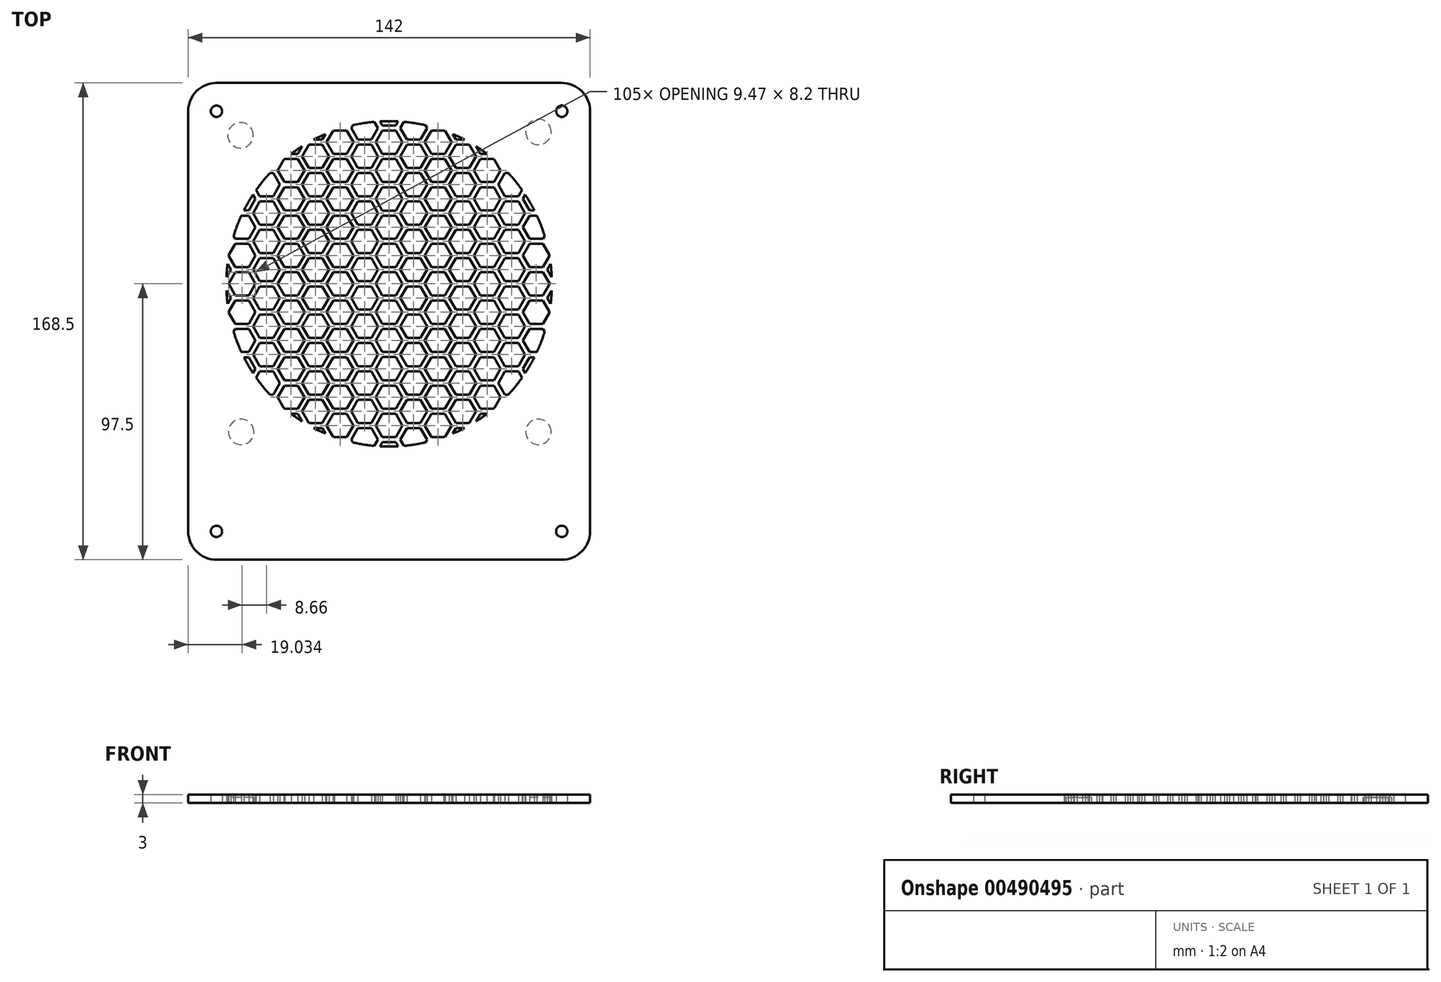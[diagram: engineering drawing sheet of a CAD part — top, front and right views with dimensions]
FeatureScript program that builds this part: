
annotation { "Feature Type Name" : "Feature", "Feature Type Description" : "" }
export const myFeature = defineFeature(function(context is Context, id is Id, definition is map)
    precondition{}
    {
        {
            var Q0;
            Q0=qCreatedBy(makeId("Top.planeOp"),FACE);
            var sketch = newSketch(context, id + "F0", { "sketchPlane" : qUnion([Q0])});
            skPoint(sketch, "E0.middle", {"position": v(0, 0) * mm});
            skLineSegment(sketch, "E1", {"start": v(-61, -92.5) * mm, "end": v(61, -92.5) * mm, "construction": true});
            skLineSegment(sketch, "E2", {"start": v(-66, 61) * mm, "end": v(-66, -87.5) * mm, "construction": true});
            skLineSegment(sketch, "E3", {"start": v(-61, 66) * mm, "end": v(61, 66) * mm, "construction": true});
            skLineSegment(sketch, "E4", {"start": v(66, 61) * mm, "end": v(66, -87.5) * mm, "construction": true});
            skArc(sketch, "E5.filletArc", {"start": v(-61, 66) * mm, "mid": v(-64.54, 64.54) * mm, "end": v(-66, 61) * mm, "construction": true});
            skArc(sketch, "E6.filletArc", {"start": v(66, 61) * mm, "mid": v(64.54, 64.54) * mm, "end": v(61, 66) * mm, "construction": true});
            skArc(sketch, "E7.converted", {"start": v(-66, -87.5) * mm, "mid": v(-64.54, -91.04) * mm, "end": v(-61, -92.5) * mm, "construction": true});
            skArc(sketch, "E8.trimOffspring", {"start": v(61, -92.5) * mm, "mid": v(64.54, -91.04) * mm, "end": v(66, -87.5) * mm, "construction": true});
            skPoint(sketch, "E9", {"position": v(-54.5, -54.5) * mm});
            skPoint(sketch, "E10", {"position": v(-54.5, 54.5) * mm});
            skPoint(sketch, "E11", {"position": v(54.5, 54.5) * mm});
            skPoint(sketch, "E12", {"position": v(54.5, -54.5) * mm});
            skLineSegment(sketch, "E13", {"start": v(-59.5, 59.5) * mm, "end": v(59.5, -59.5) * mm, "construction": true});
            skLineSegment(sketch, "E14", {"start": v(-59.5, -59.5) * mm, "end": v(59.5, 59.5) * mm, "construction": true});
            skArc(sketch, "E15", {"start": v(57.5, 0) * mm, "mid": v(57.4, 3.52) * mm, "end": v(57.07, 7.03) * mm});
            skLineSegment(sketch, "E16.0", {"start": v(3.93, 5) * mm, "end": v(6.3, 0.9) * mm});
            skLineSegment(sketch, "E16.1", {"start": v(6.3, 9.1) * mm, "end": v(11.03, 9.1) * mm});
            skLineSegment(sketch, "E16.2", {"start": v(13.4, 5) * mm, "end": v(11.03, 9.1) * mm});
            skLineSegment(sketch, "E16.3", {"start": v(3.93, 5) * mm, "end": v(6.3, 9.1) * mm});
            skLineSegment(sketch, "E16.4", {"start": v(11.03, 0.9) * mm, "end": v(13.4, 5) * mm});
            skLineSegment(sketch, "E16.5", {"start": v(6.3, 0.9) * mm, "end": v(11.03, 0.9) * mm});
            skLineSegment(sketch, "E17.1", {"start": v(14.95, 4.1) * mm, "end": v(19.69, 4.1) * mm});
            skLineSegment(sketch, "E17.2", {"start": v(22.05, 0) * mm, "end": v(19.69, 4.1) * mm});
            skLineSegment(sketch, "E17.3", {"start": v(12.59, 0) * mm, "end": v(14.95, 4.1) * mm});
            skLineSegment(sketch, "E18.0", {"start": v(21.25, 5) * mm, "end": v(23.61, 0.9) * mm});
            skLineSegment(sketch, "E18.1", {"start": v(23.61, 9.1) * mm, "end": v(28.35, 9.1) * mm});
            skLineSegment(sketch, "E18.2", {"start": v(30.72, 5) * mm, "end": v(28.35, 9.1) * mm});
            skLineSegment(sketch, "E18.3", {"start": v(21.25, 5) * mm, "end": v(23.61, 9.1) * mm});
            skLineSegment(sketch, "E18.4", {"start": v(28.35, 0.9) * mm, "end": v(30.72, 5) * mm});
            skLineSegment(sketch, "E18.5", {"start": v(23.61, 0.9) * mm, "end": v(28.35, 0.9) * mm});
            skLineSegment(sketch, "E19.1", {"start": v(32.27, 4.1) * mm, "end": v(37, 4.1) * mm});
            skLineSegment(sketch, "E19.2", {"start": v(39.38, 0) * mm, "end": v(37, 4.1) * mm});
            skLineSegment(sketch, "E19.3", {"start": v(29.9, 0) * mm, "end": v(32.27, 4.1) * mm});
            skLineSegment(sketch, "E20.0", {"start": v(38.57, 5) * mm, "end": v(40.94, 0.9) * mm});
            skLineSegment(sketch, "E20.1", {"start": v(40.94, 9.1) * mm, "end": v(45.67, 9.1) * mm});
            skLineSegment(sketch, "E20.2", {"start": v(48.04, 5) * mm, "end": v(45.67, 9.1) * mm});
            skLineSegment(sketch, "E20.3", {"start": v(38.57, 5) * mm, "end": v(40.94, 9.1) * mm});
            skLineSegment(sketch, "E20.4", {"start": v(45.67, 0.9) * mm, "end": v(48.04, 5) * mm});
            skLineSegment(sketch, "E20.5", {"start": v(40.94, 0.9) * mm, "end": v(45.67, 0.9) * mm});
            skLineSegment(sketch, "E21.1", {"start": v(49.6, 4.1) * mm, "end": v(54.33, 4.1) * mm});
            skLineSegment(sketch, "E21.2", {"start": v(56.7, 0) * mm, "end": v(54.33, 4.1) * mm});
            skLineSegment(sketch, "E21.3", {"start": v(47.23, 0) * mm, "end": v(49.6, 4.1) * mm});
            skLineSegment(sketch, "E22.0", {"start": v(55.9, 5) * mm, "end": v(57.45, 2.3) * mm});
            skLineSegment(sketch, "E22.3", {"start": v(55.9, 5) * mm, "end": v(57.07, 7.03) * mm});
            skLineSegment(sketch, "E23.1", {"start": v(0, 4.1) * mm, "end": v(2.37, 4.1) * mm});
            skLineSegment(sketch, "E23.2", {"start": v(4.73, 0) * mm, "end": v(2.37, 4.1) * mm});
            skLineSegment(sketch, "E24.1", {"start": v(0, 14.1) * mm, "end": v(2.37, 14.1) * mm});
            skLineSegment(sketch, "E24.2", {"start": v(4.73, 10) * mm, "end": v(2.37, 14.1) * mm});
            skLineSegment(sketch, "E24.4", {"start": v(2.37, 5.9) * mm, "end": v(4.73, 10) * mm});
            skLineSegment(sketch, "E24.5", {"start": v(0, 5.9) * mm, "end": v(2.37, 5.9) * mm});
            skLineSegment(sketch, "E25.0", {"start": v(3.93, 15) * mm, "end": v(6.3, 10.9) * mm});
            skLineSegment(sketch, "E25.1", {"start": v(6.3, 19.1) * mm, "end": v(11.03, 19.1) * mm});
            skLineSegment(sketch, "E25.2", {"start": v(13.4, 15) * mm, "end": v(11.03, 19.1) * mm});
            skLineSegment(sketch, "E25.3", {"start": v(3.93, 15) * mm, "end": v(6.3, 19.1) * mm});
            skLineSegment(sketch, "E25.4", {"start": v(11.03, 10.9) * mm, "end": v(13.4, 15) * mm});
            skLineSegment(sketch, "E25.5", {"start": v(6.3, 10.9) * mm, "end": v(11.03, 10.9) * mm});
            skLineSegment(sketch, "E26.0", {"start": v(12.59, 10) * mm, "end": v(14.95, 5.9) * mm});
            skLineSegment(sketch, "E26.1", {"start": v(14.95, 14.1) * mm, "end": v(19.69, 14.1) * mm});
            skLineSegment(sketch, "E26.2", {"start": v(22.05, 10) * mm, "end": v(19.69, 14.1) * mm});
            skLineSegment(sketch, "E26.3", {"start": v(12.59, 10) * mm, "end": v(14.95, 14.1) * mm});
            skLineSegment(sketch, "E26.4", {"start": v(19.69, 5.9) * mm, "end": v(22.05, 10) * mm});
            skLineSegment(sketch, "E26.5", {"start": v(14.95, 5.9) * mm, "end": v(19.69, 5.9) * mm});
            skLineSegment(sketch, "E27.0", {"start": v(21.25, 15) * mm, "end": v(23.61, 10.9) * mm});
            skLineSegment(sketch, "E27.1", {"start": v(23.61, 19.1) * mm, "end": v(28.35, 19.1) * mm});
            skLineSegment(sketch, "E27.2", {"start": v(30.72, 15) * mm, "end": v(28.35, 19.1) * mm});
            skLineSegment(sketch, "E27.3", {"start": v(21.25, 15) * mm, "end": v(23.61, 19.1) * mm});
            skLineSegment(sketch, "E27.4", {"start": v(28.35, 10.9) * mm, "end": v(30.72, 15) * mm});
            skLineSegment(sketch, "E27.5", {"start": v(23.61, 10.9) * mm, "end": v(28.35, 10.9) * mm});
            skLineSegment(sketch, "E28.0", {"start": v(29.9, 10) * mm, "end": v(32.27, 5.9) * mm});
            skLineSegment(sketch, "E28.1", {"start": v(32.27, 14.1) * mm, "end": v(37, 14.1) * mm});
            skLineSegment(sketch, "E28.2", {"start": v(39.38, 10) * mm, "end": v(37, 14.1) * mm});
            skLineSegment(sketch, "E28.3", {"start": v(29.9, 10) * mm, "end": v(32.27, 14.1) * mm});
            skLineSegment(sketch, "E28.4", {"start": v(37, 5.9) * mm, "end": v(39.38, 10) * mm});
            skLineSegment(sketch, "E28.5", {"start": v(32.27, 5.9) * mm, "end": v(37, 5.9) * mm});
            skLineSegment(sketch, "E29.0", {"start": v(38.57, 15) * mm, "end": v(40.94, 10.9) * mm});
            skLineSegment(sketch, "E29.1", {"start": v(40.94, 19.1) * mm, "end": v(45.67, 19.1) * mm});
            skLineSegment(sketch, "E29.2", {"start": v(48.04, 15) * mm, "end": v(45.67, 19.1) * mm});
            skLineSegment(sketch, "E29.3", {"start": v(38.57, 15) * mm, "end": v(40.94, 19.1) * mm});
            skLineSegment(sketch, "E29.4", {"start": v(45.67, 10.9) * mm, "end": v(48.04, 15) * mm});
            skLineSegment(sketch, "E29.5", {"start": v(40.94, 10.9) * mm, "end": v(45.67, 10.9) * mm});
            skLineSegment(sketch, "E30.0", {"start": v(47.23, 10) * mm, "end": v(49.6, 5.9) * mm});
            skLineSegment(sketch, "E30.1", {"start": v(49.6, 14.1) * mm, "end": v(54.33, 14.1) * mm});
            skLineSegment(sketch, "E30.2", {"start": v(56.59, 10.2) * mm, "end": v(54.33, 14.1) * mm});
            skLineSegment(sketch, "E30.3", {"start": v(47.23, 10) * mm, "end": v(49.6, 14.1) * mm});
            skLineSegment(sketch, "E30.4", {"start": v(54.33, 5.9) * mm, "end": v(56.64, 9.9) * mm});
            skLineSegment(sketch, "E30.5", {"start": v(49.6, 5.9) * mm, "end": v(54.33, 5.9) * mm});
            skLineSegment(sketch, "E31.1", {"start": v(0, 24.1) * mm, "end": v(2.37, 24.1) * mm});
            skLineSegment(sketch, "E31.2", {"start": v(4.73, 20) * mm, "end": v(2.37, 24.1) * mm});
            skLineSegment(sketch, "E31.4", {"start": v(2.37, 15.9) * mm, "end": v(4.73, 20) * mm});
            skLineSegment(sketch, "E31.5", {"start": v(0, 15.9) * mm, "end": v(2.37, 15.9) * mm});
            skLineSegment(sketch, "E32.0", {"start": v(3.93, 25) * mm, "end": v(6.3, 20.9) * mm});
            skLineSegment(sketch, "E32.1", {"start": v(6.3, 29.1) * mm, "end": v(11.03, 29.1) * mm});
            skLineSegment(sketch, "E32.2", {"start": v(13.4, 25) * mm, "end": v(11.03, 29.1) * mm});
            skLineSegment(sketch, "E32.3", {"start": v(3.93, 25) * mm, "end": v(6.3, 29.1) * mm});
            skLineSegment(sketch, "E32.4", {"start": v(11.03, 20.9) * mm, "end": v(13.4, 25) * mm});
            skLineSegment(sketch, "E32.5", {"start": v(6.3, 20.9) * mm, "end": v(11.03, 20.9) * mm});
            skLineSegment(sketch, "E33.0", {"start": v(12.59, 20) * mm, "end": v(14.95, 15.9) * mm});
            skLineSegment(sketch, "E33.1", {"start": v(14.95, 24.1) * mm, "end": v(19.69, 24.1) * mm});
            skLineSegment(sketch, "E33.2", {"start": v(22.05, 20) * mm, "end": v(19.69, 24.1) * mm});
            skLineSegment(sketch, "E33.3", {"start": v(12.59, 20) * mm, "end": v(14.95, 24.1) * mm});
            skLineSegment(sketch, "E33.4", {"start": v(19.69, 15.9) * mm, "end": v(22.05, 20) * mm});
            skLineSegment(sketch, "E33.5", {"start": v(14.95, 15.9) * mm, "end": v(19.69, 15.9) * mm});
            skLineSegment(sketch, "E34.0", {"start": v(21.25, 25) * mm, "end": v(23.61, 20.9) * mm});
            skLineSegment(sketch, "E34.1", {"start": v(23.61, 29.1) * mm, "end": v(28.35, 29.1) * mm});
            skLineSegment(sketch, "E34.2", {"start": v(30.72, 25) * mm, "end": v(28.35, 29.1) * mm});
            skLineSegment(sketch, "E34.3", {"start": v(21.25, 25) * mm, "end": v(23.61, 29.1) * mm});
            skLineSegment(sketch, "E34.4", {"start": v(28.35, 20.9) * mm, "end": v(30.72, 25) * mm});
            skLineSegment(sketch, "E34.5", {"start": v(23.61, 20.9) * mm, "end": v(28.35, 20.9) * mm});
            skLineSegment(sketch, "E35.0", {"start": v(29.9, 20) * mm, "end": v(32.27, 15.9) * mm});
            skLineSegment(sketch, "E35.1", {"start": v(32.27, 24.1) * mm, "end": v(37, 24.1) * mm});
            skLineSegment(sketch, "E35.2", {"start": v(39.38, 20) * mm, "end": v(37, 24.1) * mm});
            skLineSegment(sketch, "E35.3", {"start": v(29.9, 20) * mm, "end": v(32.27, 24.1) * mm});
            skLineSegment(sketch, "E35.4", {"start": v(37, 15.9) * mm, "end": v(39.38, 20) * mm});
            skLineSegment(sketch, "E35.5", {"start": v(32.27, 15.9) * mm, "end": v(37, 15.9) * mm});
            skLineSegment(sketch, "E36.0", {"start": v(38.57, 25) * mm, "end": v(40.94, 20.9) * mm});
            skLineSegment(sketch, "E36.1", {"start": v(40.94, 29.1) * mm, "end": v(45.67, 29.1) * mm});
            skLineSegment(sketch, "E36.2", {"start": v(48.04, 25) * mm, "end": v(45.67, 29.1) * mm});
            skLineSegment(sketch, "E36.3", {"start": v(38.57, 25) * mm, "end": v(40.94, 29.1) * mm});
            skLineSegment(sketch, "E36.4", {"start": v(45.67, 20.9) * mm, "end": v(48.04, 25) * mm});
            skLineSegment(sketch, "E36.5", {"start": v(40.94, 20.9) * mm, "end": v(45.67, 20.9) * mm});
            skLineSegment(sketch, "E37.0", {"start": v(47.23, 20) * mm, "end": v(49.6, 15.9) * mm});
            skLineSegment(sketch, "E37.1", {"start": v(49.6, 24.1) * mm, "end": v(52.2, 24.1) * mm});
            skLineSegment(sketch, "E37.3", {"start": v(47.23, 20) * mm, "end": v(49.6, 24.1) * mm});
            skLineSegment(sketch, "E37.4", {"start": v(54.33, 15.9) * mm, "end": v(54.94, 16.96) * mm});
            skLineSegment(sketch, "E37.5", {"start": v(49.6, 15.9) * mm, "end": v(54.33, 15.9) * mm});
            skLineSegment(sketch, "E38.1", {"start": v(0, 34.1) * mm, "end": v(2.37, 34.1) * mm});
            skLineSegment(sketch, "E38.2", {"start": v(4.73, 30) * mm, "end": v(2.37, 34.1) * mm});
            skLineSegment(sketch, "E38.4", {"start": v(2.37, 25.9) * mm, "end": v(4.73, 30) * mm});
            skLineSegment(sketch, "E38.5", {"start": v(0, 25.9) * mm, "end": v(2.37, 25.9) * mm});
            skLineSegment(sketch, "E39.0", {"start": v(3.93, 35.06) * mm, "end": v(6.3, 30.96) * mm});
            skLineSegment(sketch, "E39.1", {"start": v(6.3, 39.16) * mm, "end": v(11.03, 39.16) * mm});
            skLineSegment(sketch, "E39.2", {"start": v(13.4, 35.06) * mm, "end": v(11.03, 39.16) * mm});
            skLineSegment(sketch, "E39.3", {"start": v(3.93, 35.06) * mm, "end": v(6.3, 39.16) * mm});
            skLineSegment(sketch, "E39.4", {"start": v(11.03, 30.96) * mm, "end": v(13.4, 35.06) * mm});
            skLineSegment(sketch, "E39.5", {"start": v(6.3, 30.96) * mm, "end": v(11.03, 30.96) * mm});
            skLineSegment(sketch, "E40.0", {"start": v(12.59, 30.06) * mm, "end": v(14.95, 25.96) * mm});
            skLineSegment(sketch, "E40.1", {"start": v(14.95, 34.16) * mm, "end": v(19.69, 34.16) * mm});
            skLineSegment(sketch, "E40.2", {"start": v(22.05, 30.06) * mm, "end": v(19.69, 34.16) * mm});
            skLineSegment(sketch, "E40.3", {"start": v(12.59, 30.06) * mm, "end": v(14.95, 34.16) * mm});
            skLineSegment(sketch, "E40.4", {"start": v(19.69, 25.96) * mm, "end": v(22.05, 30.06) * mm});
            skLineSegment(sketch, "E40.5", {"start": v(14.95, 25.96) * mm, "end": v(19.69, 25.96) * mm});
            skLineSegment(sketch, "E41.0", {"start": v(21.25, 35.06) * mm, "end": v(23.61, 30.96) * mm});
            skLineSegment(sketch, "E41.1", {"start": v(23.61, 39.16) * mm, "end": v(28.35, 39.16) * mm});
            skLineSegment(sketch, "E41.2", {"start": v(30.72, 35.06) * mm, "end": v(28.35, 39.16) * mm});
            skLineSegment(sketch, "E41.3", {"start": v(21.25, 35.06) * mm, "end": v(23.61, 39.16) * mm});
            skLineSegment(sketch, "E41.4", {"start": v(28.35, 30.96) * mm, "end": v(30.72, 35.06) * mm});
            skLineSegment(sketch, "E41.5", {"start": v(23.61, 30.96) * mm, "end": v(28.35, 30.96) * mm});
            skLineSegment(sketch, "E42.0", {"start": v(29.9, 30.06) * mm, "end": v(32.27, 25.96) * mm});
            skLineSegment(sketch, "E42.1", {"start": v(32.27, 34.16) * mm, "end": v(37, 34.16) * mm});
            skLineSegment(sketch, "E42.2", {"start": v(39.38, 30.06) * mm, "end": v(37, 34.16) * mm});
            skLineSegment(sketch, "E42.3", {"start": v(29.9, 30.06) * mm, "end": v(32.27, 34.16) * mm});
            skLineSegment(sketch, "E42.4", {"start": v(37, 25.96) * mm, "end": v(39.38, 30.06) * mm});
            skLineSegment(sketch, "E42.5", {"start": v(32.27, 25.96) * mm, "end": v(37, 25.96) * mm});
            skLineSegment(sketch, "E43.0", {"start": v(38.57, 35.06) * mm, "end": v(40.94, 30.96) * mm});
            skLineSegment(sketch, "E43.1", {"start": v(40.94, 39.16) * mm, "end": v(42.1, 39.16) * mm});
            skLineSegment(sketch, "E43.3", {"start": v(38.57, 35.06) * mm, "end": v(40.94, 39.16) * mm});
            skLineSegment(sketch, "E43.4", {"start": v(45.67, 30.96) * mm, "end": v(46.96, 33.18) * mm});
            skLineSegment(sketch, "E43.5", {"start": v(40.94, 30.96) * mm, "end": v(45.67, 30.96) * mm});
            skLineSegment(sketch, "E44.0", {"start": v(47.23, 30.06) * mm, "end": v(49.6, 25.96) * mm});
            skLineSegment(sketch, "E44.3", {"start": v(47.23, 30.06) * mm, "end": v(48.08, 31.53) * mm});
            skLineSegment(sketch, "E44.5", {"start": v(49.6, 25.96) * mm, "end": v(51.3, 25.96) * mm});
            skLineSegment(sketch, "E45.1", {"start": v(0, 44.16) * mm, "end": v(2.37, 44.16) * mm});
            skLineSegment(sketch, "E45.2", {"start": v(4.73, 40.06) * mm, "end": v(2.37, 44.16) * mm});
            skLineSegment(sketch, "E45.4", {"start": v(2.37, 35.96) * mm, "end": v(4.73, 40.06) * mm});
            skLineSegment(sketch, "E45.5", {"start": v(0, 35.96) * mm, "end": v(2.37, 35.96) * mm});
            skLineSegment(sketch, "E46.0", {"start": v(3.93, 45.06) * mm, "end": v(6.3, 40.96) * mm});
            skLineSegment(sketch, "E46.1", {"start": v(6.3, 49.16) * mm, "end": v(11.03, 49.16) * mm});
            skLineSegment(sketch, "E46.2", {"start": v(13.4, 45.06) * mm, "end": v(11.03, 49.16) * mm});
            skLineSegment(sketch, "E46.3", {"start": v(3.93, 45.06) * mm, "end": v(6.3, 49.16) * mm});
            skLineSegment(sketch, "E46.4", {"start": v(11.03, 40.96) * mm, "end": v(13.4, 45.06) * mm});
            skLineSegment(sketch, "E46.5", {"start": v(6.3, 40.96) * mm, "end": v(11.03, 40.96) * mm});
            skLineSegment(sketch, "E47.0", {"start": v(12.59, 40.06) * mm, "end": v(14.95, 35.96) * mm});
            skLineSegment(sketch, "E47.1", {"start": v(14.95, 44.16) * mm, "end": v(19.69, 44.16) * mm});
            skLineSegment(sketch, "E47.2", {"start": v(22.05, 40.06) * mm, "end": v(19.69, 44.16) * mm});
            skLineSegment(sketch, "E47.3", {"start": v(12.59, 40.06) * mm, "end": v(14.95, 44.16) * mm});
            skLineSegment(sketch, "E47.4", {"start": v(19.69, 35.96) * mm, "end": v(22.05, 40.06) * mm});
            skLineSegment(sketch, "E47.5", {"start": v(14.95, 35.96) * mm, "end": v(19.69, 35.96) * mm});
            skLineSegment(sketch, "E48.0", {"start": v(21.25, 45.06) * mm, "end": v(23.61, 40.96) * mm});
            skLineSegment(sketch, "E48.1", {"start": v(23.61, 49.16) * mm, "end": v(28.35, 49.16) * mm});
            skLineSegment(sketch, "E48.2", {"start": v(30.72, 45.06) * mm, "end": v(28.35, 49.16) * mm});
            skLineSegment(sketch, "E48.3", {"start": v(21.25, 45.06) * mm, "end": v(23.61, 49.16) * mm});
            skLineSegment(sketch, "E48.4", {"start": v(28.35, 40.96) * mm, "end": v(30.72, 45.06) * mm});
            skLineSegment(sketch, "E48.5", {"start": v(23.61, 40.96) * mm, "end": v(28.35, 40.96) * mm});
            skLineSegment(sketch, "E49.0", {"start": v(29.9, 40.06) * mm, "end": v(32.27, 35.96) * mm});
            skLineSegment(sketch, "E49.1", {"start": v(32.27, 44.16) * mm, "end": v(36.83, 44.16) * mm});
            skLineSegment(sketch, "E49.2", {"start": v(39.38, 40.06) * mm, "end": v(37.18, 43.86) * mm});
            skLineSegment(sketch, "E49.3", {"start": v(29.9, 40.06) * mm, "end": v(32.27, 44.16) * mm});
            skLineSegment(sketch, "E49.4", {"start": v(37, 35.96) * mm, "end": v(39.38, 40.06) * mm});
            skLineSegment(sketch, "E49.5", {"start": v(32.27, 35.96) * mm, "end": v(37, 35.96) * mm});
            skLineSegment(sketch, "E50.1", {"start": v(0, 54.16) * mm, "end": v(2.37, 54.16) * mm});
            skLineSegment(sketch, "E50.2", {"start": v(4.73, 50.06) * mm, "end": v(2.37, 54.16) * mm});
            skLineSegment(sketch, "E50.4", {"start": v(2.37, 45.96) * mm, "end": v(4.73, 50.06) * mm});
            skLineSegment(sketch, "E50.5", {"start": v(0, 45.96) * mm, "end": v(2.37, 45.96) * mm});
            skLineSegment(sketch, "E51.0", {"start": v(3.93, 55.06) * mm, "end": v(6.3, 50.96) * mm});
            skLineSegment(sketch, "E51.2", {"start": v(13.4, 55.06) * mm, "end": v(12.82, 56.05) * mm});
            skLineSegment(sketch, "E51.3", {"start": v(3.93, 55.06) * mm, "end": v(5.2, 57.26) * mm});
            skLineSegment(sketch, "E51.4", {"start": v(11.03, 50.96) * mm, "end": v(13.4, 55.06) * mm});
            skLineSegment(sketch, "E51.5", {"start": v(6.3, 50.96) * mm, "end": v(11.03, 50.96) * mm});
            skLineSegment(sketch, "E52.0", {"start": v(12.59, 50.06) * mm, "end": v(14.95, 45.96) * mm});
            skLineSegment(sketch, "E52.1", {"start": v(14.95, 54.16) * mm, "end": v(19.32, 54.16) * mm});
            skLineSegment(sketch, "E52.2", {"start": v(22.05, 50.06) * mm, "end": v(19.79, 53.99) * mm});
            skLineSegment(sketch, "E52.3", {"start": v(12.59, 50.06) * mm, "end": v(14.95, 54.16) * mm});
            skLineSegment(sketch, "E52.4", {"start": v(19.69, 45.96) * mm, "end": v(22.05, 50.06) * mm});
            skLineSegment(sketch, "E52.5", {"start": v(14.95, 45.96) * mm, "end": v(19.69, 45.96) * mm});
            skLineSegment(sketch, "E53.0", {"start": v(22.48, 52.92) * mm, "end": v(23.61, 50.96) * mm});
            skLineSegment(sketch, "E53.5", {"start": v(23.61, 50.96) * mm, "end": v(26.64, 50.96) * mm});
            skLineSegment(sketch, "E54.0", {"start": v(30.76, 48.58) * mm, "end": v(32.27, 45.96) * mm});
            skLineSegment(sketch, "E54.5", {"start": v(32.27, 45.96) * mm, "end": v(34.56, 45.96) * mm});
            skLineSegment(sketch, "E55.MirrorCS", {"start": v(-45.67, 30.96) * mm, "end": v(-46.96, 33.18) * mm});
            skLineSegment(sketch, "E56.MirrorCS", {"start": v(-6.3, 19.1) * mm, "end": v(-11.03, 19.1) * mm});
            skLineSegment(sketch, "E57.MirrorCS", {"start": v(0, 15.9) * mm, "end": v(-2.37, 15.9) * mm});
            skLineSegment(sketch, "E58.MirrorCS", {"start": v(-28.35, 20.9) * mm, "end": v(-30.72, 25) * mm});
            skLineSegment(sketch, "E59.MirrorCS", {"start": v(-29.9, 40.06) * mm, "end": v(-32.27, 44.16) * mm});
            skLineSegment(sketch, "E60.MirrorCS", {"start": v(-14.95, 34.16) * mm, "end": v(-19.69, 34.16) * mm});
            skLineSegment(sketch, "E61.MirrorCS", {"start": v(-21.25, 15) * mm, "end": v(-23.61, 10.9) * mm});
            skLineSegment(sketch, "E62.MirrorCS", {"start": v(-40.94, 29.1) * mm, "end": v(-45.67, 29.1) * mm});
            skLineSegment(sketch, "E63.MirrorCS", {"start": v(-14.95, 5.9) * mm, "end": v(-19.69, 5.9) * mm});
            skLineSegment(sketch, "E64.MirrorCS", {"start": v(-38.57, 15) * mm, "end": v(-40.94, 19.1) * mm});
            skLineSegment(sketch, "E65.MirrorCS", {"start": v(-3.93, 45.06) * mm, "end": v(-6.3, 49.16) * mm});
            skLineSegment(sketch, "E66.MirrorCS", {"start": v(-56.59, 10.2) * mm, "end": v(-54.33, 14.1) * mm});
            skLineSegment(sketch, "E67.MirrorCS", {"start": v(-4.73, 40.06) * mm, "end": v(-2.37, 44.16) * mm});
            skLineSegment(sketch, "E68.MirrorCS", {"start": v(-11.03, 50.96) * mm, "end": v(-13.4, 55.06) * mm});
            skLineSegment(sketch, "E69.MirrorCS", {"start": v(-2.37, 45.96) * mm, "end": v(-4.73, 50.06) * mm});
            skLineSegment(sketch, "E70.MirrorCS", {"start": v(-32.27, 34.16) * mm, "end": v(-37, 34.16) * mm});
            skLineSegment(sketch, "E71.MirrorCS", {"start": v(-3.93, 35.06) * mm, "end": v(-6.3, 39.16) * mm});
            skLineSegment(sketch, "E72.MirrorCS", {"start": v(0, 35.96) * mm, "end": v(-2.37, 35.96) * mm});
            skLineSegment(sketch, "E73.MirrorCS", {"start": v(-47.23, 30.06) * mm, "end": v(-49.6, 25.96) * mm});
            skLineSegment(sketch, "E74.MirrorCS", {"start": v(-29.9, 10) * mm, "end": v(-32.27, 5.9) * mm});
            skLineSegment(sketch, "E75.MirrorCS", {"start": v(-21.25, 45.06) * mm, "end": v(-23.61, 49.16) * mm});
            skLineSegment(sketch, "E76.MirrorCS", {"start": v(-22.05, 50.06) * mm, "end": v(-19.79, 53.99) * mm});
            skLineSegment(sketch, "E77.MirrorCS", {"start": v(-37, 35.96) * mm, "end": v(-39.38, 40.06) * mm});
            skLineSegment(sketch, "E78.MirrorCS", {"start": v(-38.57, 15) * mm, "end": v(-40.94, 10.9) * mm});
            skLineSegment(sketch, "E79.MirrorCS", {"start": v(-22.05, 20) * mm, "end": v(-19.69, 24.1) * mm});
            skLineSegment(sketch, "E80.MirrorCS", {"start": v(-32.27, 5.9) * mm, "end": v(-37, 5.9) * mm});
            skLineSegment(sketch, "E81.MirrorCS", {"start": v(-39.38, 10) * mm, "end": v(-37, 14.1) * mm});
            skLineSegment(sketch, "E82.MirrorCS", {"start": v(-32.27, 45.96) * mm, "end": v(-34.56, 45.96) * mm});
            skLineSegment(sketch, "E83.MirrorCS", {"start": v(-12.59, 50.06) * mm, "end": v(-14.95, 54.16) * mm});
            skLineSegment(sketch, "E84.MirrorCS", {"start": v(-30.72, 5) * mm, "end": v(-28.35, 9.1) * mm});
            skLineSegment(sketch, "E85.MirrorCS", {"start": v(-21.25, 25) * mm, "end": v(-23.61, 20.9) * mm});
            skLineSegment(sketch, "E86.MirrorCS", {"start": v(-45.67, 20.9) * mm, "end": v(-48.04, 25) * mm});
            skLineSegment(sketch, "E87.MirrorCS", {"start": v(-40.94, 39.16) * mm, "end": v(-42.1, 39.16) * mm});
            skLineSegment(sketch, "E88.MirrorCS", {"start": v(-45.67, 10.9) * mm, "end": v(-48.04, 15) * mm});
            skLineSegment(sketch, "E89.MirrorCS", {"start": v(0, 25.9) * mm, "end": v(-2.37, 25.9) * mm});
            skLineSegment(sketch, "E90.MirrorCS", {"start": v(-22.05, 0) * mm, "end": v(-19.69, 4.1) * mm});
            skLineSegment(sketch, "E91.MirrorCS", {"start": v(-29.9, 20) * mm, "end": v(-32.27, 15.9) * mm});
            skLineSegment(sketch, "E92.MirrorCS", {"start": v(-21.25, 25) * mm, "end": v(-23.61, 29.1) * mm});
            skLineSegment(sketch, "E93.MirrorCS", {"start": v(0, 44.16) * mm, "end": v(-2.37, 44.16) * mm});
            skLineSegment(sketch, "E94.MirrorCS", {"start": v(-38.57, 35.06) * mm, "end": v(-40.94, 39.16) * mm});
            skLineSegment(sketch, "E95.MirrorCS", {"start": v(-13.4, 25) * mm, "end": v(-11.03, 29.1) * mm});
            skLineSegment(sketch, "E96.MirrorCS", {"start": v(-55.9, 5) * mm, "end": v(-57.07, 7.03) * mm});
            skLineSegment(sketch, "E97.MirrorCS", {"start": v(-47.23, 10) * mm, "end": v(-49.6, 14.1) * mm});
            skLineSegment(sketch, "E98.MirrorCS", {"start": v(-32.27, 24.1) * mm, "end": v(-37, 24.1) * mm});
            skLineSegment(sketch, "E99.MirrorCS", {"start": v(-3.93, 25) * mm, "end": v(-6.3, 20.9) * mm});
            skLineSegment(sketch, "E100.MirrorCS", {"start": v(-40.94, 0.9) * mm, "end": v(-45.67, 0.9) * mm});
            skLineSegment(sketch, "E101.MirrorCS", {"start": v(-40.94, 19.1) * mm, "end": v(-45.67, 19.1) * mm});
            skLineSegment(sketch, "E102.MirrorCS", {"start": v(-6.3, 9.1) * mm, "end": v(-11.03, 9.1) * mm});
            skLineSegment(sketch, "E103.MirrorCS", {"start": v(-49.6, 15.9) * mm, "end": v(-54.33, 15.9) * mm});
            skLineSegment(sketch, "E104.MirrorCS", {"start": v(-14.95, 25.96) * mm, "end": v(-19.69, 25.96) * mm});
            skLineSegment(sketch, "E105.MirrorCS", {"start": v(-28.35, 0.9) * mm, "end": v(-30.72, 5) * mm});
            skLineSegment(sketch, "E106.MirrorCS", {"start": v(-38.57, 25) * mm, "end": v(-40.94, 20.9) * mm});
            skLineSegment(sketch, "E107.MirrorCS", {"start": v(-19.69, 5.9) * mm, "end": v(-22.05, 10) * mm});
            skLineSegment(sketch, "E108.MirrorCS", {"start": v(0, 4.1) * mm, "end": v(-2.37, 4.1) * mm});
            skLineSegment(sketch, "E109.MirrorCS", {"start": v(-23.61, 50.96) * mm, "end": v(-26.64, 50.96) * mm});
            skLineSegment(sketch, "E110.MirrorCS", {"start": v(-48.04, 15) * mm, "end": v(-45.67, 19.1) * mm});
            skLineSegment(sketch, "E111.MirrorCS", {"start": v(-23.61, 10.9) * mm, "end": v(-28.35, 10.9) * mm});
            skLineSegment(sketch, "E112.MirrorCS", {"start": v(-3.93, 15) * mm, "end": v(-6.3, 19.1) * mm});
            skLineSegment(sketch, "E113.MirrorCS", {"start": v(-40.94, 10.9) * mm, "end": v(-45.67, 10.9) * mm});
            skLineSegment(sketch, "E114.MirrorCS", {"start": v(-47.23, 10) * mm, "end": v(-49.6, 5.9) * mm});
            skLineSegment(sketch, "E115.MirrorCS", {"start": v(-23.61, 19.1) * mm, "end": v(-28.35, 19.1) * mm});
            skLineSegment(sketch, "E116.MirrorCS", {"start": v(-54.33, 15.9) * mm, "end": v(-54.94, 16.96) * mm});
            skLineSegment(sketch, "E117.MirrorCS", {"start": v(-49.6, 24.1) * mm, "end": v(-52.2, 24.1) * mm});
            skLineSegment(sketch, "E118.MirrorCS", {"start": v(-4.73, 50.06) * mm, "end": v(-2.37, 54.16) * mm});
            skLineSegment(sketch, "E119.MirrorCS", {"start": v(-14.95, 24.1) * mm, "end": v(-19.69, 24.1) * mm});
            skLineSegment(sketch, "E120.MirrorCS", {"start": v(-11.03, 40.96) * mm, "end": v(-13.4, 45.06) * mm});
            skLineSegment(sketch, "E121.MirrorCS", {"start": v(-39.38, 40.06) * mm, "end": v(-37.18, 43.86) * mm});
            skLineSegment(sketch, "E122.MirrorCS", {"start": v(-22.05, 30.06) * mm, "end": v(-19.69, 34.16) * mm});
            skLineSegment(sketch, "E123.MirrorCS", {"start": v(-45.67, 0.9) * mm, "end": v(-48.04, 5) * mm});
            skLineSegment(sketch, "E124.MirrorCS", {"start": v(-14.95, 4.1) * mm, "end": v(-19.69, 4.1) * mm});
            skLineSegment(sketch, "E125.MirrorCS", {"start": v(-14.95, 15.9) * mm, "end": v(-19.69, 15.9) * mm});
            skLineSegment(sketch, "E126.MirrorCS", {"start": v(-30.72, 15) * mm, "end": v(-28.35, 19.1) * mm});
            skLineSegment(sketch, "E127.MirrorCS", {"start": v(-3.93, 25) * mm, "end": v(-6.3, 29.1) * mm});
            skLineSegment(sketch, "E128.MirrorCS", {"start": v(-23.61, 9.1) * mm, "end": v(-28.35, 9.1) * mm});
            skLineSegment(sketch, "E129.MirrorCS", {"start": v(-38.57, 25) * mm, "end": v(-40.94, 29.1) * mm});
            skLineSegment(sketch, "E130.MirrorCS", {"start": v(-3.93, 5) * mm, "end": v(-6.3, 0.9) * mm});
            skLineSegment(sketch, "E131.MirrorCS", {"start": v(-21.25, 5) * mm, "end": v(-23.61, 9.1) * mm});
            skLineSegment(sketch, "E132.MirrorCS", {"start": v(-23.61, 20.9) * mm, "end": v(-28.35, 20.9) * mm});
            skLineSegment(sketch, "E133.MirrorCS", {"start": v(-23.61, 30.96) * mm, "end": v(-28.35, 30.96) * mm});
            skLineSegment(sketch, "E134.MirrorCS", {"start": v(0, 45.96) * mm, "end": v(-2.37, 45.96) * mm});
            skLineSegment(sketch, "E135.MirrorCS", {"start": v(-4.73, 0) * mm, "end": v(-2.37, 4.1) * mm});
            skLineSegment(sketch, "E136.MirrorCS", {"start": v(-19.69, 25.96) * mm, "end": v(-22.05, 30.06) * mm});
            skLineSegment(sketch, "E137.MirrorCS", {"start": v(-32.27, 15.9) * mm, "end": v(-37, 15.9) * mm});
            skLineSegment(sketch, "E138.MirrorCS", {"start": v(-14.95, 35.96) * mm, "end": v(-19.69, 35.96) * mm});
            skLineSegment(sketch, "E139.MirrorCS", {"start": v(-12.59, 20) * mm, "end": v(-14.95, 15.9) * mm});
            skLineSegment(sketch, "E140.MirrorCS", {"start": v(-48.04, 5) * mm, "end": v(-45.67, 9.1) * mm});
            skLineSegment(sketch, "E141.MirrorCS", {"start": v(-47.23, 20) * mm, "end": v(-49.6, 24.1) * mm});
            skLineSegment(sketch, "E142.MirrorCS", {"start": v(-29.9, 30.06) * mm, "end": v(-32.27, 25.96) * mm});
            skLineSegment(sketch, "E143.MirrorCS", {"start": v(-3.93, 55.06) * mm, "end": v(-5.2, 57.26) * mm});
            skLineSegment(sketch, "E144.MirrorCS", {"start": v(0, 24.1) * mm, "end": v(-2.37, 24.1) * mm});
            skLineSegment(sketch, "E145.MirrorCS", {"start": v(-14.95, 14.1) * mm, "end": v(-19.69, 14.1) * mm});
            skLineSegment(sketch, "E146.MirrorCS", {"start": v(-23.61, 40.96) * mm, "end": v(-28.35, 40.96) * mm});
            skLineSegment(sketch, "E147.MirrorCS", {"start": v(-6.3, 29.1) * mm, "end": v(-11.03, 29.1) * mm});
            skLineSegment(sketch, "E148.MirrorCS", {"start": v(-49.6, 5.9) * mm, "end": v(-54.33, 5.9) * mm});
            skLineSegment(sketch, "E149.MirrorCS", {"start": v(-29.9, 30.06) * mm, "end": v(-32.27, 34.16) * mm});
            skLineSegment(sketch, "E150.MirrorCS", {"start": v(-6.3, 49.16) * mm, "end": v(-11.03, 49.16) * mm});
            skLineSegment(sketch, "E151.MirrorCS", {"start": v(-32.27, 14.1) * mm, "end": v(-37, 14.1) * mm});
            skLineSegment(sketch, "E152.MirrorCS", {"start": v(-12.59, 50.06) * mm, "end": v(-14.95, 45.96) * mm});
            skLineSegment(sketch, "E153.MirrorCS", {"start": v(-37, 5.9) * mm, "end": v(-39.38, 10) * mm});
            skLineSegment(sketch, "E154.MirrorCS", {"start": v(-28.35, 40.96) * mm, "end": v(-30.72, 45.06) * mm});
            skLineSegment(sketch, "E155.MirrorCS", {"start": v(-39.38, 30.06) * mm, "end": v(-37, 34.16) * mm});
            skLineSegment(sketch, "E156.MirrorCS", {"start": v(-21.25, 45.06) * mm, "end": v(-23.61, 40.96) * mm});
            skLineSegment(sketch, "E157.MirrorCS", {"start": v(-32.27, 35.96) * mm, "end": v(-37, 35.96) * mm});
            skLineSegment(sketch, "E158.MirrorCS", {"start": v(-40.94, 9.1) * mm, "end": v(-45.67, 9.1) * mm});
            skLineSegment(sketch, "E159.MirrorCS", {"start": v(-12.59, 40.06) * mm, "end": v(-14.95, 44.16) * mm});
            skLineSegment(sketch, "E160.MirrorCS", {"start": v(-3.93, 45.06) * mm, "end": v(-6.3, 40.96) * mm});
            skLineSegment(sketch, "E161.MirrorCS", {"start": v(-38.57, 5) * mm, "end": v(-40.94, 0.9) * mm});
            skLineSegment(sketch, "E162.MirrorCS", {"start": v(-6.3, 30.96) * mm, "end": v(-11.03, 30.96) * mm});
            skLineSegment(sketch, "E163.MirrorCS", {"start": v(-6.3, 50.96) * mm, "end": v(-11.03, 50.96) * mm});
            skLineSegment(sketch, "E164.MirrorCS", {"start": v(-47.23, 20) * mm, "end": v(-49.6, 15.9) * mm});
            skLineSegment(sketch, "E165.MirrorCS", {"start": v(-19.69, 35.96) * mm, "end": v(-22.05, 40.06) * mm});
            skLineSegment(sketch, "E166.MirrorCS", {"start": v(-54.33, 5.9) * mm, "end": v(-56.64, 9.9) * mm});
            skLineSegment(sketch, "E167.MirrorCS", {"start": v(-29.9, 0) * mm, "end": v(-32.27, 4.1) * mm});
            skLineSegment(sketch, "E168.MirrorCS", {"start": v(-23.61, 49.16) * mm, "end": v(-28.35, 49.16) * mm});
            skLineSegment(sketch, "E169.MirrorCS", {"start": v(-2.37, 25.9) * mm, "end": v(-4.73, 30) * mm});
            skLineSegment(sketch, "E170.MirrorCS", {"start": v(-12.59, 30.06) * mm, "end": v(-14.95, 34.16) * mm});
            skLineSegment(sketch, "E171.MirrorCS", {"start": v(-32.27, 4.1) * mm, "end": v(-37, 4.1) * mm});
            skLineSegment(sketch, "E172.MirrorCS", {"start": v(-38.57, 5) * mm, "end": v(-40.94, 9.1) * mm});
            skLineSegment(sketch, "E173.MirrorCS", {"start": v(-38.57, 35.06) * mm, "end": v(-40.94, 30.96) * mm});
            skLineSegment(sketch, "E174.MirrorCS", {"start": v(-13.4, 55.06) * mm, "end": v(-12.82, 56.05) * mm});
            skLineSegment(sketch, "E175.MirrorCS", {"start": v(-4.73, 10) * mm, "end": v(-2.37, 14.1) * mm});
            skLineSegment(sketch, "E176.MirrorCS", {"start": v(-49.6, 25.96) * mm, "end": v(-51.3, 25.96) * mm});
            skLineSegment(sketch, "E177.MirrorCS", {"start": v(-12.59, 0) * mm, "end": v(-14.95, 4.1) * mm});
            skLineSegment(sketch, "E178.MirrorCS", {"start": v(-12.59, 10) * mm, "end": v(-14.95, 5.9) * mm});
            skLineSegment(sketch, "E179.MirrorCS", {"start": v(-49.6, 4.1) * mm, "end": v(-54.33, 4.1) * mm});
            skLineSegment(sketch, "E180.MirrorCS", {"start": v(-40.94, 20.9) * mm, "end": v(-45.67, 20.9) * mm});
            skLineSegment(sketch, "E181.MirrorCS", {"start": v(-32.27, 44.16) * mm, "end": v(-36.83, 44.16) * mm});
            skLineSegment(sketch, "E182.MirrorCS", {"start": v(-47.23, 30.06) * mm, "end": v(-48.08, 31.53) * mm});
            skLineSegment(sketch, "E183.MirrorCS", {"start": v(0, 54.16) * mm, "end": v(-2.37, 54.16) * mm});
            skLineSegment(sketch, "E184.MirrorCS", {"start": v(-12.59, 20) * mm, "end": v(-14.95, 24.1) * mm});
            skLineSegment(sketch, "E185.MirrorCS", {"start": v(-6.3, 10.9) * mm, "end": v(-11.03, 10.9) * mm});
            skLineSegment(sketch, "E186.MirrorCS", {"start": v(-56.7, 0) * mm, "end": v(-54.33, 4.1) * mm});
            skLineSegment(sketch, "E187.MirrorCS", {"start": v(0, 14.1) * mm, "end": v(-2.37, 14.1) * mm});
            skLineSegment(sketch, "E188.MirrorCS", {"start": v(-21.25, 5) * mm, "end": v(-23.61, 0.9) * mm});
            skLineSegment(sketch, "E189.MirrorCS", {"start": v(-12.59, 10) * mm, "end": v(-14.95, 14.1) * mm});
            skLineSegment(sketch, "E190.MirrorCS", {"start": v(-19.69, 15.9) * mm, "end": v(-22.05, 20) * mm});
            skLineSegment(sketch, "E191.MirrorCS", {"start": v(-11.03, 30.96) * mm, "end": v(-13.4, 35.06) * mm});
            skLineSegment(sketch, "E192.MirrorCS", {"start": v(-3.93, 35.06) * mm, "end": v(-6.3, 30.96) * mm});
            skLineSegment(sketch, "E193.MirrorCS", {"start": v(-23.61, 29.1) * mm, "end": v(-28.35, 29.1) * mm});
            skLineSegment(sketch, "E194.MirrorCS", {"start": v(-4.73, 20) * mm, "end": v(-2.37, 24.1) * mm});
            skLineSegment(sketch, "E195.MirrorCS", {"start": v(-30.72, 45.06) * mm, "end": v(-28.35, 49.16) * mm});
            skLineSegment(sketch, "E196.MirrorCS", {"start": v(-11.03, 20.9) * mm, "end": v(-13.4, 25) * mm});
            skLineSegment(sketch, "E197.MirrorCS", {"start": v(-37, 25.96) * mm, "end": v(-39.38, 30.06) * mm});
            skLineSegment(sketch, "E198.MirrorCS", {"start": v(-21.25, 35.06) * mm, "end": v(-23.61, 39.16) * mm});
            skLineSegment(sketch, "E199.MirrorCS", {"start": v(-4.73, 30) * mm, "end": v(-2.37, 34.1) * mm});
            skLineSegment(sketch, "E200.MirrorCS", {"start": v(-37, 15.9) * mm, "end": v(-39.38, 20) * mm});
            skLineSegment(sketch, "E201.MirrorCS", {"start": v(-48.04, 25) * mm, "end": v(-45.67, 29.1) * mm});
            skLineSegment(sketch, "E202.MirrorCS", {"start": v(-2.37, 35.96) * mm, "end": v(-4.73, 40.06) * mm});
            skLineSegment(sketch, "E203.MirrorCS", {"start": v(-3.93, 55.06) * mm, "end": v(-6.3, 50.96) * mm});
            skLineSegment(sketch, "E204.MirrorCS", {"start": v(-12.59, 40.06) * mm, "end": v(-14.95, 35.96) * mm});
            skLineSegment(sketch, "E205.MirrorCS", {"start": v(-6.3, 40.96) * mm, "end": v(-11.03, 40.96) * mm});
            skLineSegment(sketch, "E206.MirrorCS", {"start": v(-6.3, 39.16) * mm, "end": v(-11.03, 39.16) * mm});
            skLineSegment(sketch, "E207.MirrorCS", {"start": v(-21.25, 15) * mm, "end": v(-23.61, 19.1) * mm});
            skLineSegment(sketch, "E208.MirrorCS", {"start": v(-14.95, 44.16) * mm, "end": v(-19.69, 44.16) * mm});
            skLineSegment(sketch, "E209.MirrorCS", {"start": v(-13.4, 15) * mm, "end": v(-11.03, 19.1) * mm});
            skLineSegment(sketch, "E210.MirrorCS", {"start": v(-2.37, 5.9) * mm, "end": v(-4.73, 10) * mm});
            skLineSegment(sketch, "E211.MirrorCS", {"start": v(-28.35, 10.9) * mm, "end": v(-30.72, 15) * mm});
            skLineSegment(sketch, "E212.MirrorCS", {"start": v(-30.72, 25) * mm, "end": v(-28.35, 29.1) * mm});
            skLineSegment(sketch, "E213.MirrorCS", {"start": v(-2.37, 15.9) * mm, "end": v(-4.73, 20) * mm});
            skLineSegment(sketch, "E214.MirrorCS", {"start": v(-6.3, 20.9) * mm, "end": v(-11.03, 20.9) * mm});
            skLineSegment(sketch, "E215.MirrorCS", {"start": v(-32.27, 25.96) * mm, "end": v(-37, 25.96) * mm});
            skLineSegment(sketch, "E216.MirrorCS", {"start": v(-6.3, 0.9) * mm, "end": v(-11.03, 0.9) * mm});
            skLineSegment(sketch, "E217.MirrorCS", {"start": v(-13.4, 5) * mm, "end": v(-11.03, 9.1) * mm});
            skLineSegment(sketch, "E218.MirrorCS", {"start": v(-30.76, 48.58) * mm, "end": v(-32.27, 45.96) * mm});
            skLineSegment(sketch, "E219.MirrorCS", {"start": v(-30.72, 35.06) * mm, "end": v(-28.35, 39.16) * mm});
            skLineSegment(sketch, "E220.MirrorCS", {"start": v(-3.93, 15) * mm, "end": v(-6.3, 10.9) * mm});
            skLineSegment(sketch, "E221.MirrorCS", {"start": v(-13.4, 35.06) * mm, "end": v(-11.03, 39.16) * mm});
            skLineSegment(sketch, "E222.MirrorCS", {"start": v(-29.9, 20) * mm, "end": v(-32.27, 24.1) * mm});
            skLineSegment(sketch, "E223.MirrorCS", {"start": v(-13.4, 45.06) * mm, "end": v(-11.03, 49.16) * mm});
            skLineSegment(sketch, "E224.MirrorCS", {"start": v(-29.9, 40.06) * mm, "end": v(-32.27, 35.96) * mm});
            skLineSegment(sketch, "E225.MirrorCS", {"start": v(-11.03, 10.9) * mm, "end": v(-13.4, 15) * mm});
            skLineSegment(sketch, "E226.MirrorCS", {"start": v(0, 34.1) * mm, "end": v(-2.37, 34.1) * mm});
            skLineSegment(sketch, "E227.MirrorCS", {"start": v(-12.59, 30.06) * mm, "end": v(-14.95, 25.96) * mm});
            skLineSegment(sketch, "E228.MirrorCS", {"start": v(-22.05, 10) * mm, "end": v(-19.69, 14.1) * mm});
            skLineSegment(sketch, "E229.MirrorCS", {"start": v(-47.23, 0) * mm, "end": v(-49.6, 4.1) * mm});
            skLineSegment(sketch, "E230.MirrorCS", {"start": v(-19.69, 45.96) * mm, "end": v(-22.05, 50.06) * mm});
            skLineSegment(sketch, "E231.MirrorCS", {"start": v(-39.38, 20) * mm, "end": v(-37, 24.1) * mm});
            skLineSegment(sketch, "E232.MirrorCS", {"start": v(-28.35, 30.96) * mm, "end": v(-30.72, 35.06) * mm});
            skLineSegment(sketch, "E233.MirrorCS", {"start": v(-23.61, 0.9) * mm, "end": v(-28.35, 0.9) * mm});
            skLineSegment(sketch, "E234.MirrorCS", {"start": v(-23.61, 39.16) * mm, "end": v(-28.35, 39.16) * mm});
            skLineSegment(sketch, "E235.MirrorCS", {"start": v(0, 5.9) * mm, "end": v(-2.37, 5.9) * mm});
            skLineSegment(sketch, "E236.MirrorCS", {"start": v(-39.38, 0) * mm, "end": v(-37, 4.1) * mm});
            skLineSegment(sketch, "E237.MirrorCS", {"start": v(-49.6, 14.1) * mm, "end": v(-54.33, 14.1) * mm});
            skLineSegment(sketch, "E238.MirrorCS", {"start": v(-22.05, 40.06) * mm, "end": v(-19.69, 44.16) * mm});
            skLineSegment(sketch, "E239.MirrorCS", {"start": v(-3.93, 5) * mm, "end": v(-6.3, 9.1) * mm});
            skLineSegment(sketch, "E240.MirrorCS", {"start": v(-29.9, 10) * mm, "end": v(-32.27, 14.1) * mm});
            skLineSegment(sketch, "E241.MirrorCS", {"start": v(-14.95, 54.16) * mm, "end": v(-19.32, 54.16) * mm});
            skLineSegment(sketch, "E242.MirrorCS", {"start": v(-11.03, 0.9) * mm, "end": v(-13.4, 5) * mm});
            skLineSegment(sketch, "E243.MirrorCS", {"start": v(-55.9, 5) * mm, "end": v(-57.45, 2.3) * mm});
            skLineSegment(sketch, "E244.MirrorCS", {"start": v(-40.94, 30.96) * mm, "end": v(-45.67, 30.96) * mm});
            skLineSegment(sketch, "E245.MirrorCS", {"start": v(-14.95, 45.96) * mm, "end": v(-19.69, 45.96) * mm});
            skLineSegment(sketch, "E246.MirrorCS", {"start": v(-21.25, 35.06) * mm, "end": v(-23.61, 30.96) * mm});
            skLineSegment(sketch, "E247.MirrorCS", {"start": v(0, -15.9) * mm, "end": v(-2.37, -15.9) * mm});
            skLineSegment(sketch, "E248.MirrorCS", {"start": v(0, -4.1) * mm, "end": v(-2.37, -4.1) * mm});
            skLineSegment(sketch, "E249.MirrorCS", {"start": v(0, -25.9) * mm, "end": v(-2.37, -25.9) * mm});
            skLineSegment(sketch, "E250.MirrorCS", {"start": v(0, -14.1) * mm, "end": v(-2.37, -14.1) * mm});
            skLineSegment(sketch, "E251.MirrorCS", {"start": v(0, -44.16) * mm, "end": v(2.37, -44.16) * mm});
            skLineSegment(sketch, "E252.MirrorCS", {"start": v(0, -35.96) * mm, "end": v(-2.37, -35.96) * mm});
            skLineSegment(sketch, "E253.MirrorCS", {"start": v(0, -34.1) * mm, "end": v(2.37, -34.1) * mm});
            skLineSegment(sketch, "E254.MirrorCS", {"start": v(0, -45.96) * mm, "end": v(2.37, -45.96) * mm});
            skLineSegment(sketch, "E255.MirrorCS", {"start": v(0, -24.1) * mm, "end": v(-2.37, -24.1) * mm});
            skLineSegment(sketch, "E256.MirrorCS", {"start": v(0, -15.9) * mm, "end": v(2.37, -15.9) * mm});
            skLineSegment(sketch, "E257.MirrorCS", {"start": v(0, -45.96) * mm, "end": v(-2.37, -45.96) * mm});
            skLineSegment(sketch, "E258.MirrorCS", {"start": v(0, -35.96) * mm, "end": v(2.37, -35.96) * mm});
            skLineSegment(sketch, "E259.MirrorCS", {"start": v(0, -5.9) * mm, "end": v(-2.37, -5.9) * mm});
            skLineSegment(sketch, "E260.MirrorCS", {"start": v(0, -25.9) * mm, "end": v(2.37, -25.9) * mm});
            skLineSegment(sketch, "E261.MirrorCS", {"start": v(0, -44.16) * mm, "end": v(-2.37, -44.16) * mm});
            skLineSegment(sketch, "E262.MirrorCS", {"start": v(0, -34.1) * mm, "end": v(-2.37, -34.1) * mm});
            skLineSegment(sketch, "E263.MirrorCS", {"start": v(0, -4.1) * mm, "end": v(2.37, -4.1) * mm});
            skLineSegment(sketch, "E264.MirrorCS", {"start": v(0, -55.96) * mm, "end": v(2.37, -55.96) * mm});
            skLineSegment(sketch, "E265.MirrorCS", {"start": v(0, -54.16) * mm, "end": v(-2.37, -54.16) * mm});
            skLineSegment(sketch, "E266.MirrorCS", {"start": v(0, -14.1) * mm, "end": v(2.37, -14.1) * mm});
            skLineSegment(sketch, "E267.MirrorCS", {"start": v(0, -24.1) * mm, "end": v(2.37, -24.1) * mm});
            skLineSegment(sketch, "E268.MirrorCS", {"start": v(0, -55.96) * mm, "end": v(-2.37, -55.96) * mm});
            skLineSegment(sketch, "E269.MirrorCS", {"start": v(0, -5.9) * mm, "end": v(2.37, -5.9) * mm});
            skLineSegment(sketch, "E270.MirrorCS", {"start": v(0, -54.16) * mm, "end": v(2.37, -54.16) * mm});
            skLineSegment(sketch, "E271.MirrorCS", {"start": v(-37, -35.96) * mm, "end": v(-39.38, -40.06) * mm});
            skLineSegment(sketch, "E272.MirrorCS", {"start": v(-14.95, -4.1) * mm, "end": v(-19.69, -4.1) * mm});
            skLineSegment(sketch, "E273.MirrorCS", {"start": v(-12.59, 0) * mm, "end": v(-14.95, -4.1) * mm});
            skLineSegment(sketch, "E274.MirrorCS", {"start": v(-14.95, -5.9) * mm, "end": v(-19.69, -5.9) * mm});
            skLineSegment(sketch, "E275.MirrorCS", {"start": v(-11.03, -0.9) * mm, "end": v(-13.4, -5) * mm});
            skLineSegment(sketch, "E276.MirrorCS", {"start": v(-39.38, -40.06) * mm, "end": v(-37.18, -43.86) * mm});
            skLineSegment(sketch, "E277.MirrorCS", {"start": v(-48.04, -15) * mm, "end": v(-45.67, -19.1) * mm});
            skLineSegment(sketch, "E278.MirrorCS", {"start": v(-28.35, -0.9) * mm, "end": v(-30.72, -5) * mm});
            skLineSegment(sketch, "E279.MirrorCS", {"start": v(47.23, -20) * mm, "end": v(49.6, -15.9) * mm});
            skLineSegment(sketch, "E280.MirrorCS", {"start": v(-11.03, -40.96) * mm, "end": v(-13.4, -45.06) * mm});
            skLineSegment(sketch, "E281.MirrorCS", {"start": v(30.72, -35.06) * mm, "end": v(28.35, -39.16) * mm});
            skLineSegment(sketch, "E282.MirrorCS", {"start": v(29.9, -40.06) * mm, "end": v(32.27, -44.16) * mm});
            skLineSegment(sketch, "E283.MirrorCS", {"start": v(49.6, -25.96) * mm, "end": v(51.3, -25.96) * mm});
            skLineSegment(sketch, "E284.MirrorCS", {"start": v(-45.67, -0.9) * mm, "end": v(-48.04, -5) * mm});
            skLineSegment(sketch, "E285.MirrorCS", {"start": v(-32.27, -44.16) * mm, "end": v(-36.83, -44.16) * mm});
            skLineSegment(sketch, "E286.MirrorCS", {"start": v(48.04, -15) * mm, "end": v(45.67, -19.1) * mm});
            skLineSegment(sketch, "E287.MirrorCS", {"start": v(40.94, -9.1) * mm, "end": v(45.67, -9.1) * mm});
            skLineSegment(sketch, "E288.MirrorCS", {"start": v(39.38, -20) * mm, "end": v(37, -24.1) * mm});
            skLineSegment(sketch, "E289.MirrorCS", {"start": v(-19.69, -25.96) * mm, "end": v(-22.05, -30.06) * mm});
            skLineSegment(sketch, "E290.MirrorCS", {"start": v(21.25, -15) * mm, "end": v(23.61, -10.9) * mm});
            skLineSegment(sketch, "E291.MirrorCS", {"start": v(-12.59, -50.06) * mm, "end": v(-14.95, -45.96) * mm});
            skLineSegment(sketch, "E292.MirrorCS", {"start": v(-6.3, -9.1) * mm, "end": v(-11.03, -9.1) * mm});
            skLineSegment(sketch, "E293.MirrorCS", {"start": v(32.27, -4.1) * mm, "end": v(37, -4.1) * mm});
            skLineSegment(sketch, "E294.MirrorCS", {"start": v(14.95, -54.16) * mm, "end": v(19.32, -54.16) * mm});
            skLineSegment(sketch, "E295.MirrorCS", {"start": v(-21.25, -45.06) * mm, "end": v(-23.61, -49.16) * mm});
            skLineSegment(sketch, "E296.MirrorCS", {"start": v(-29.9, -40.06) * mm, "end": v(-32.27, -44.16) * mm});
            skLineSegment(sketch, "E297.MirrorCS", {"start": v(-12.59, -20) * mm, "end": v(-14.95, -24.1) * mm});
            skLineSegment(sketch, "E298.MirrorCS", {"start": v(-6.3, -0.9) * mm, "end": v(-11.03, -0.9) * mm});
            skLineSegment(sketch, "E299.MirrorCS", {"start": v(12.59, -30.06) * mm, "end": v(14.95, -25.96) * mm});
            skLineSegment(sketch, "E300.MirrorCS", {"start": v(-23.61, -49.16) * mm, "end": v(-28.35, -49.16) * mm});
            skLineSegment(sketch, "E301.MirrorCS", {"start": v(-37, -15.9) * mm, "end": v(-39.38, -20) * mm});
            skLineSegment(sketch, "E302.MirrorCS", {"start": v(30.76, -48.58) * mm, "end": v(32.27, -45.96) * mm});
            skLineSegment(sketch, "E303.MirrorCS", {"start": v(-49.6, -5.9) * mm, "end": v(-54.33, -5.9) * mm});
            skLineSegment(sketch, "E304.MirrorCS", {"start": v(3.93, -55.06) * mm, "end": v(6.3, -50.96) * mm});
            skLineSegment(sketch, "E305.MirrorCS", {"start": v(-13.4, -5) * mm, "end": v(-11.03, -9.1) * mm});
            skLineSegment(sketch, "E306.MirrorCS", {"start": v(-6.3, -19.1) * mm, "end": v(-11.03, -19.1) * mm});
            skLineSegment(sketch, "E307.MirrorCS", {"start": v(30.72, -15) * mm, "end": v(28.35, -19.1) * mm});
            skLineSegment(sketch, "E308.MirrorCS", {"start": v(-6.3, -29.1) * mm, "end": v(-11.03, -29.1) * mm});
            skLineSegment(sketch, "E309.MirrorCS", {"start": v(-23.61, -29.1) * mm, "end": v(-28.35, -29.1) * mm});
            skLineSegment(sketch, "E310.MirrorCS", {"start": v(32.27, -34.16) * mm, "end": v(37, -34.16) * mm});
            skLineSegment(sketch, "E311.MirrorCS", {"start": v(40.94, -30.96) * mm, "end": v(45.67, -30.96) * mm});
            skLineSegment(sketch, "E312.MirrorCS", {"start": v(-47.23, -10) * mm, "end": v(-49.6, -14.1) * mm});
            skLineSegment(sketch, "E313.MirrorCS", {"start": v(-49.6, -4.1) * mm, "end": v(-54.33, -4.1) * mm});
            skLineSegment(sketch, "E314.MirrorCS", {"start": v(3.93, -5) * mm, "end": v(6.3, -9.1) * mm});
            skLineSegment(sketch, "E315.MirrorCS", {"start": v(-12.59, -10) * mm, "end": v(-14.95, -5.9) * mm});
            skLineSegment(sketch, "E316.MirrorCS", {"start": v(11.03, -10.9) * mm, "end": v(13.4, -15) * mm});
            skLineSegment(sketch, "E317.MirrorCS", {"start": v(-23.61, -40.96) * mm, "end": v(-28.35, -40.96) * mm});
            skLineSegment(sketch, "E318.MirrorCS", {"start": v(-28.35, -30.96) * mm, "end": v(-30.72, -35.06) * mm});
            skLineSegment(sketch, "E319.MirrorCS", {"start": v(37, -25.96) * mm, "end": v(39.38, -30.06) * mm});
            skLineSegment(sketch, "E320.MirrorCS", {"start": v(13.4, -45.06) * mm, "end": v(11.03, -49.16) * mm});
            skLineSegment(sketch, "E321.MirrorCS", {"start": v(29.9, -40.06) * mm, "end": v(32.27, -35.96) * mm});
            skLineSegment(sketch, "E322.MirrorCS", {"start": v(29.9, -10) * mm, "end": v(32.27, -14.1) * mm});
            skLineSegment(sketch, "E323.MirrorCS", {"start": v(4.73, -20) * mm, "end": v(2.37, -24.1) * mm});
            skLineSegment(sketch, "E324.MirrorCS", {"start": v(14.95, -4.1) * mm, "end": v(19.69, -4.1) * mm});
            skLineSegment(sketch, "E325.MirrorCS", {"start": v(40.94, -20.9) * mm, "end": v(45.67, -20.9) * mm});
            skLineSegment(sketch, "E326.MirrorCS", {"start": v(23.61, -29.1) * mm, "end": v(28.35, -29.1) * mm});
            skLineSegment(sketch, "E327.MirrorCS", {"start": v(12.59, 0) * mm, "end": v(14.95, -4.1) * mm});
            skLineSegment(sketch, "E328.MirrorCS", {"start": v(13.4, -35.06) * mm, "end": v(11.03, -39.16) * mm});
            skLineSegment(sketch, "E329.MirrorCS", {"start": v(-29.9, -30.06) * mm, "end": v(-32.27, -25.96) * mm});
            skLineSegment(sketch, "E330.MirrorCS", {"start": v(6.3, -10.9) * mm, "end": v(11.03, -10.9) * mm});
            skLineSegment(sketch, "E331.MirrorCS", {"start": v(49.6, -4.1) * mm, "end": v(54.33, -4.1) * mm});
            skLineSegment(sketch, "E332.MirrorCS", {"start": v(56.7, 0) * mm, "end": v(54.33, -4.1) * mm});
            skLineSegment(sketch, "E333.MirrorCS", {"start": v(-21.25, -35.06) * mm, "end": v(-23.61, -30.96) * mm});
            skLineSegment(sketch, "E334.MirrorCS", {"start": v(-39.38, -20) * mm, "end": v(-37, -24.1) * mm});
            skLineSegment(sketch, "E335.MirrorCS", {"start": v(4.73, -40.06) * mm, "end": v(2.37, -44.16) * mm});
            skLineSegment(sketch, "E336.MirrorCS", {"start": v(-48.04, -5) * mm, "end": v(-45.67, -9.1) * mm});
            skLineSegment(sketch, "E337.MirrorCS", {"start": v(38.57, -15) * mm, "end": v(40.94, -10.9) * mm});
            skLineSegment(sketch, "E338.MirrorCS", {"start": v(22.05, -10) * mm, "end": v(19.69, -14.1) * mm});
            skLineSegment(sketch, "E339.MirrorCS", {"start": v(-47.23, -30.06) * mm, "end": v(-48.08, -31.53) * mm});
            skLineSegment(sketch, "E340.MirrorCS", {"start": v(28.35, -0.9) * mm, "end": v(30.72, -5) * mm});
            skLineSegment(sketch, "E341.MirrorCS", {"start": v(-12.59, -50.06) * mm, "end": v(-14.95, -54.16) * mm});
            skLineSegment(sketch, "E342.MirrorCS", {"start": v(56.59, -10.2) * mm, "end": v(54.33, -14.1) * mm});
            skLineSegment(sketch, "E343.MirrorCS", {"start": v(32.27, -14.1) * mm, "end": v(37, -14.1) * mm});
            skLineSegment(sketch, "E344.MirrorCS", {"start": v(13.4, -5) * mm, "end": v(11.03, -9.1) * mm});
            skLineSegment(sketch, "E345.MirrorCS", {"start": v(55.9, -5) * mm, "end": v(57.45, -2.3) * mm});
            skLineSegment(sketch, "E346.MirrorCS", {"start": v(-13.4, -25) * mm, "end": v(-11.03, -29.1) * mm});
            skLineSegment(sketch, "E347.MirrorCS", {"start": v(-22.05, -40.06) * mm, "end": v(-19.69, -44.16) * mm});
            skLineSegment(sketch, "E348.MirrorCS", {"start": v(-38.57, -25) * mm, "end": v(-40.94, -20.9) * mm});
            skLineSegment(sketch, "E349.MirrorCS", {"start": v(30.72, -5) * mm, "end": v(28.35, -9.1) * mm});
            skLineSegment(sketch, "E350.MirrorCS", {"start": v(6.3, -9.1) * mm, "end": v(11.03, -9.1) * mm});
            skLineSegment(sketch, "E351.MirrorCS", {"start": v(4.73, -10) * mm, "end": v(2.37, -14.1) * mm});
            skLineSegment(sketch, "E352.MirrorCS", {"start": v(22.05, -30.06) * mm, "end": v(19.69, -34.16) * mm});
            skLineSegment(sketch, "E353.MirrorCS", {"start": v(-14.95, -54.16) * mm, "end": v(-19.32, -54.16) * mm});
            skLineSegment(sketch, "E354.MirrorCS", {"start": v(-32.27, -35.96) * mm, "end": v(-37, -35.96) * mm});
            skLineSegment(sketch, "E355.MirrorCS", {"start": v(-21.25, -15) * mm, "end": v(-23.61, -10.9) * mm});
            skLineSegment(sketch, "E356.MirrorCS", {"start": v(-38.57, -15) * mm, "end": v(-40.94, -19.1) * mm});
            skLineSegment(sketch, "E357.MirrorCS", {"start": v(-3.93, -45.06) * mm, "end": v(-6.3, -40.96) * mm});
            skLineSegment(sketch, "E358.MirrorCS", {"start": v(-4.73, -10) * mm, "end": v(-2.37, -14.1) * mm});
            skLineSegment(sketch, "E359.MirrorCS", {"start": v(40.94, -10.9) * mm, "end": v(45.67, -10.9) * mm});
            skLineSegment(sketch, "E360.MirrorCS", {"start": v(49.6, -24.1) * mm, "end": v(52.2, -24.1) * mm});
            skLineSegment(sketch, "E361.MirrorCS", {"start": v(23.61, -39.16) * mm, "end": v(28.35, -39.16) * mm});
            skLineSegment(sketch, "E362.MirrorCS", {"start": v(12.59, -20) * mm, "end": v(14.95, -24.1) * mm});
            skLineSegment(sketch, "E363.MirrorCS", {"start": v(-12.59, -40.06) * mm, "end": v(-14.95, -44.16) * mm});
            skLineSegment(sketch, "E364.MirrorCS", {"start": v(-6.3, -20.9) * mm, "end": v(-11.03, -20.9) * mm});
            skLineSegment(sketch, "E365.MirrorCS", {"start": v(39.38, -40.06) * mm, "end": v(37.18, -43.86) * mm});
            skLineSegment(sketch, "E366.MirrorCS", {"start": v(-3.93, -55.06) * mm, "end": v(-5.2, -57.26) * mm});
            skLineSegment(sketch, "E367.MirrorCS", {"start": v(-14.95, -15.9) * mm, "end": v(-19.69, -15.9) * mm});
            skLineSegment(sketch, "E368.MirrorCS", {"start": v(-40.94, -0.9) * mm, "end": v(-45.67, -0.9) * mm});
            skLineSegment(sketch, "E369.MirrorCS", {"start": v(21.25, -25) * mm, "end": v(23.61, -29.1) * mm});
            skLineSegment(sketch, "E370.MirrorCS", {"start": v(45.67, -0.9) * mm, "end": v(48.04, -5) * mm});
            skLineSegment(sketch, "E371.MirrorCS", {"start": v(-3.93, -25) * mm, "end": v(-6.3, -29.1) * mm});
            skLineSegment(sketch, "E372.MirrorCS", {"start": v(-3.93, -5) * mm, "end": v(-6.3, -9.1) * mm});
            skLineSegment(sketch, "E373.MirrorCS", {"start": v(-13.4, -45.06) * mm, "end": v(-11.03, -49.16) * mm});
            skLineSegment(sketch, "E374.MirrorCS", {"start": v(6.3, -20.9) * mm, "end": v(11.03, -20.9) * mm});
            skLineSegment(sketch, "E375.MirrorCS", {"start": v(-14.95, -14.1) * mm, "end": v(-19.69, -14.1) * mm});
            skLineSegment(sketch, "E376.MirrorCS", {"start": v(38.57, -5) * mm, "end": v(40.94, -0.9) * mm});
            skLineSegment(sketch, "E377.MirrorCS", {"start": v(-14.95, -44.16) * mm, "end": v(-19.69, -44.16) * mm});
            skLineSegment(sketch, "E378.MirrorCS", {"start": v(37, -35.96) * mm, "end": v(39.38, -40.06) * mm});
            skLineSegment(sketch, "E379.MirrorCS", {"start": v(40.94, -39.16) * mm, "end": v(42.1, -39.16) * mm});
            skLineSegment(sketch, "E380.MirrorCS", {"start": v(6.3, -50.96) * mm, "end": v(11.03, -50.96) * mm});
            skLineSegment(sketch, "E381.MirrorCS", {"start": v(-21.25, -15) * mm, "end": v(-23.61, -19.1) * mm});
            skLineSegment(sketch, "E382.MirrorCS", {"start": v(6.3, -19.1) * mm, "end": v(11.03, -19.1) * mm});
            skLineSegment(sketch, "E383.MirrorCS", {"start": v(37, -5.9) * mm, "end": v(39.38, -10) * mm});
            skLineSegment(sketch, "E384.MirrorCS", {"start": v(-55.9, -5) * mm, "end": v(-57.07, -7.03) * mm});
            skLineSegment(sketch, "E385.MirrorCS", {"start": v(11.03, -50.96) * mm, "end": v(13.4, -55.06) * mm});
            skLineSegment(sketch, "E386.MirrorCS", {"start": v(-30.72, -25) * mm, "end": v(-28.35, -29.1) * mm});
            skLineSegment(sketch, "E387.MirrorCS", {"start": v(-3.93, -55.06) * mm, "end": v(-6.3, -50.96) * mm});
            skLineSegment(sketch, "E388.MirrorCS", {"start": v(22.05, -20) * mm, "end": v(19.69, -24.1) * mm});
            skLineSegment(sketch, "E389.MirrorCS", {"start": v(2.37, -35.96) * mm, "end": v(4.73, -40.06) * mm});
            skLineSegment(sketch, "E390.MirrorCS", {"start": v(-32.27, -45.96) * mm, "end": v(-34.56, -45.96) * mm});
            skLineSegment(sketch, "E391.MirrorCS", {"start": v(-21.25, -5) * mm, "end": v(-23.61, -0.9) * mm});
            skLineSegment(sketch, "E392.MirrorCS", {"start": v(39.38, -30.06) * mm, "end": v(37, -34.16) * mm});
            skLineSegment(sketch, "E393.MirrorCS", {"start": v(3.93, -45.06) * mm, "end": v(6.3, -40.96) * mm});
            skLineSegment(sketch, "E394.MirrorCS", {"start": v(-21.25, -5) * mm, "end": v(-23.61, -9.1) * mm});
            skLineSegment(sketch, "E395.MirrorCS", {"start": v(14.95, -34.16) * mm, "end": v(19.69, -34.16) * mm});
            skLineSegment(sketch, "E396.MirrorCS", {"start": v(-39.38, -10) * mm, "end": v(-37, -14.1) * mm});
            skLineSegment(sketch, "E397.MirrorCS", {"start": v(-23.61, -20.9) * mm, "end": v(-28.35, -20.9) * mm});
            skLineSegment(sketch, "E398.MirrorCS", {"start": v(-12.59, -30.06) * mm, "end": v(-14.95, -34.16) * mm});
            skLineSegment(sketch, "E399.MirrorCS", {"start": v(38.57, -5) * mm, "end": v(40.94, -9.1) * mm});
            skLineSegment(sketch, "E400.MirrorCS", {"start": v(-6.3, -40.96) * mm, "end": v(-11.03, -40.96) * mm});
            skLineSegment(sketch, "E401.MirrorCS", {"start": v(-40.94, -29.1) * mm, "end": v(-45.67, -29.1) * mm});
            skLineSegment(sketch, "E402.MirrorCS", {"start": v(-11.03, -30.96) * mm, "end": v(-13.4, -35.06) * mm});
            skLineSegment(sketch, "E403.MirrorCS", {"start": v(-3.93, -45.06) * mm, "end": v(-6.3, -49.16) * mm});
            skLineSegment(sketch, "E404.MirrorCS", {"start": v(30.72, -45.06) * mm, "end": v(28.35, -49.16) * mm});
            skLineSegment(sketch, "E405.MirrorCS", {"start": v(2.37, -45.96) * mm, "end": v(4.73, -50.06) * mm});
            skLineSegment(sketch, "E406.MirrorCS", {"start": v(-32.27, -5.9) * mm, "end": v(-37, -5.9) * mm});
            skLineSegment(sketch, "E407.MirrorCS", {"start": v(12.59, -10) * mm, "end": v(14.95, -5.9) * mm});
            skLineSegment(sketch, "E408.MirrorCS", {"start": v(-40.94, -30.96) * mm, "end": v(-45.67, -30.96) * mm});
            skLineSegment(sketch, "E409.MirrorCS", {"start": v(2.37, -55.96) * mm, "end": v(3.2, -57.41) * mm});
            skLineSegment(sketch, "E410.MirrorCS", {"start": v(3.93, -15) * mm, "end": v(6.3, -10.9) * mm});
            skLineSegment(sketch, "E411.MirrorCS", {"start": v(40.94, -29.1) * mm, "end": v(45.67, -29.1) * mm});
            skLineSegment(sketch, "E412.MirrorCS", {"start": v(-6.3, -39.16) * mm, "end": v(-11.03, -39.16) * mm});
            skLineSegment(sketch, "E413.MirrorCS", {"start": v(19.69, -25.96) * mm, "end": v(22.05, -30.06) * mm});
            skLineSegment(sketch, "E414.MirrorCS", {"start": v(38.57, -35.06) * mm, "end": v(40.94, -39.16) * mm});
            skLineSegment(sketch, "E415.MirrorCS", {"start": v(-22.05, 0) * mm, "end": v(-19.69, -4.1) * mm});
            skLineSegment(sketch, "E416.MirrorCS", {"start": v(-6.3, -49.16) * mm, "end": v(-11.03, -49.16) * mm});
            skLineSegment(sketch, "E417.MirrorCS", {"start": v(-47.23, -10) * mm, "end": v(-49.6, -5.9) * mm});
            skLineSegment(sketch, "E418.MirrorCS", {"start": v(-13.4, -35.06) * mm, "end": v(-11.03, -39.16) * mm});
            skLineSegment(sketch, "E419.MirrorCS", {"start": v(22.05, -50.06) * mm, "end": v(19.79, -53.99) * mm});
            skLineSegment(sketch, "E420.MirrorCS", {"start": v(2.37, -25.9) * mm, "end": v(4.73, -30) * mm});
            skLineSegment(sketch, "E421.MirrorCS", {"start": v(28.35, -40.96) * mm, "end": v(30.72, -45.06) * mm});
            skLineSegment(sketch, "E422.MirrorCS", {"start": v(-23.61, -0.9) * mm, "end": v(-28.35, -0.9) * mm});
            skLineSegment(sketch, "E423.MirrorCS", {"start": v(32.27, -5.9) * mm, "end": v(37, -5.9) * mm});
            skLineSegment(sketch, "E424.MirrorCS", {"start": v(-29.9, -40.06) * mm, "end": v(-32.27, -35.96) * mm});
            skLineSegment(sketch, "E425.MirrorCS", {"start": v(-23.61, -30.96) * mm, "end": v(-28.35, -30.96) * mm});
            skLineSegment(sketch, "E426.MirrorCS", {"start": v(54.33, -15.9) * mm, "end": v(54.94, -16.96) * mm});
            skLineSegment(sketch, "E427.MirrorCS", {"start": v(-21.25, -25) * mm, "end": v(-23.61, -20.9) * mm});
            skLineSegment(sketch, "E428.MirrorCS", {"start": v(-38.57, -5) * mm, "end": v(-40.94, -0.9) * mm});
            skLineSegment(sketch, "E429.MirrorCS", {"start": v(22.05, 0) * mm, "end": v(19.69, -4.1) * mm});
            skLineSegment(sketch, "E430.MirrorCS", {"start": v(-30.72, -15) * mm, "end": v(-28.35, -19.1) * mm});
            skLineSegment(sketch, "E431.MirrorCS", {"start": v(-29.9, -20) * mm, "end": v(-32.27, -24.1) * mm});
            skLineSegment(sketch, "E432.MirrorCS", {"start": v(-32.27, -4.1) * mm, "end": v(-37, -4.1) * mm});
            skLineSegment(sketch, "E433.MirrorCS", {"start": v(-4.73, -20) * mm, "end": v(-2.37, -24.1) * mm});
            skLineSegment(sketch, "E434.MirrorCS", {"start": v(-14.95, -45.96) * mm, "end": v(-19.69, -45.96) * mm});
            skLineSegment(sketch, "E435.MirrorCS", {"start": v(12.59, -20) * mm, "end": v(14.95, -15.9) * mm});
            skLineSegment(sketch, "E436.MirrorCS", {"start": v(-49.6, -25.96) * mm, "end": v(-51.3, -25.96) * mm});
            skLineSegment(sketch, "E437.MirrorCS", {"start": v(29.9, -20) * mm, "end": v(32.27, -24.1) * mm});
            skLineSegment(sketch, "E438.MirrorCS", {"start": v(-28.35, -40.96) * mm, "end": v(-30.72, -45.06) * mm});
            skLineSegment(sketch, "E439.MirrorCS", {"start": v(-11.03, -10.9) * mm, "end": v(-13.4, -15) * mm});
            skLineSegment(sketch, "E440.MirrorCS", {"start": v(-6.3, -50.96) * mm, "end": v(-11.03, -50.96) * mm});
            skLineSegment(sketch, "E441.MirrorCS", {"start": v(21.25, -35.06) * mm, "end": v(23.61, -39.16) * mm});
            skLineSegment(sketch, "E442.MirrorCS", {"start": v(29.9, -10) * mm, "end": v(32.27, -5.9) * mm});
            skLineSegment(sketch, "E443.MirrorCS", {"start": v(-30.72, -45.06) * mm, "end": v(-28.35, -49.16) * mm});
            skLineSegment(sketch, "E444.MirrorCS", {"start": v(-56.7, 0) * mm, "end": v(-54.33, -4.1) * mm});
            skLineSegment(sketch, "E445.MirrorCS", {"start": v(14.95, -44.16) * mm, "end": v(19.69, -44.16) * mm});
            skLineSegment(sketch, "E446.MirrorCS", {"start": v(32.27, -15.9) * mm, "end": v(37, -15.9) * mm});
            skLineSegment(sketch, "E447.MirrorCS", {"start": v(-47.23, -20) * mm, "end": v(-49.6, -15.9) * mm});
            skLineSegment(sketch, "E448.MirrorCS", {"start": v(45.67, -20.9) * mm, "end": v(48.04, -25) * mm});
            skLineSegment(sketch, "E449.MirrorCS", {"start": v(-12.59, -10) * mm, "end": v(-14.95, -14.1) * mm});
            skLineSegment(sketch, "E450.MirrorCS", {"start": v(47.23, -30.06) * mm, "end": v(48.08, -31.53) * mm});
            skLineSegment(sketch, "E451.MirrorCS", {"start": v(-23.61, -9.1) * mm, "end": v(-28.35, -9.1) * mm});
            skLineSegment(sketch, "E452.MirrorCS", {"start": v(32.27, -25.96) * mm, "end": v(37, -25.96) * mm});
            skLineSegment(sketch, "E453.MirrorCS", {"start": v(6.3, -29.1) * mm, "end": v(11.03, -29.1) * mm});
            skLineSegment(sketch, "E454.MirrorCS", {"start": v(32.27, -44.16) * mm, "end": v(36.83, -44.16) * mm});
            skLineSegment(sketch, "E455.MirrorCS", {"start": v(30.72, -25) * mm, "end": v(28.35, -29.1) * mm});
            skLineSegment(sketch, "E456.MirrorCS", {"start": v(32.27, -35.96) * mm, "end": v(37, -35.96) * mm});
            skLineSegment(sketch, "E457.MirrorCS", {"start": v(12.59, -40.06) * mm, "end": v(14.95, -44.16) * mm});
            skLineSegment(sketch, "E458.MirrorCS", {"start": v(14.95, -35.96) * mm, "end": v(19.69, -35.96) * mm});
            skLineSegment(sketch, "E459.MirrorCS", {"start": v(3.93, -55.06) * mm, "end": v(5.2, -57.26) * mm});
            skLineSegment(sketch, "E460.MirrorCS", {"start": v(-32.27, -34.16) * mm, "end": v(-37, -34.16) * mm});
            skLineSegment(sketch, "E461.MirrorCS", {"start": v(-2.37, -15.9) * mm, "end": v(-4.73, -20) * mm});
            skLineSegment(sketch, "E462.MirrorCS", {"start": v(-23.61, -50.96) * mm, "end": v(-26.64, -50.96) * mm});
            skLineSegment(sketch, "E463.MirrorCS", {"start": v(37, -15.9) * mm, "end": v(39.38, -20) * mm});
            skLineSegment(sketch, "E464.MirrorCS", {"start": v(-38.57, -35.06) * mm, "end": v(-40.94, -30.96) * mm});
            skLineSegment(sketch, "E465.MirrorCS", {"start": v(-40.94, -10.9) * mm, "end": v(-45.67, -10.9) * mm});
            skLineSegment(sketch, "E466.MirrorCS", {"start": v(-55.9, -5) * mm, "end": v(-57.45, -2.3) * mm});
            skLineSegment(sketch, "E467.MirrorCS", {"start": v(49.6, -5.9) * mm, "end": v(54.33, -5.9) * mm});
            skLineSegment(sketch, "E468.MirrorCS", {"start": v(3.93, -5) * mm, "end": v(6.3, -0.9) * mm});
            skLineSegment(sketch, "E469.MirrorCS", {"start": v(-12.59, -20) * mm, "end": v(-14.95, -15.9) * mm});
            skLineSegment(sketch, "E470.MirrorCS", {"start": v(-21.25, -45.06) * mm, "end": v(-23.61, -40.96) * mm});
            skLineSegment(sketch, "E471.MirrorCS", {"start": v(-21.25, -25) * mm, "end": v(-23.61, -29.1) * mm});
            skLineSegment(sketch, "E472.MirrorCS", {"start": v(3.93, -35.06) * mm, "end": v(6.3, -39.16) * mm});
            skLineSegment(sketch, "E473.MirrorCS", {"start": v(-2.37, -5.9) * mm, "end": v(-4.73, -10) * mm});
            skLineSegment(sketch, "E474.MirrorCS", {"start": v(-29.9, -10) * mm, "end": v(-32.27, -14.1) * mm});
            skLineSegment(sketch, "E475.MirrorCS", {"start": v(23.61, -9.1) * mm, "end": v(28.35, -9.1) * mm});
            skLineSegment(sketch, "E476.MirrorCS", {"start": v(-2.37, -35.96) * mm, "end": v(-4.73, -40.06) * mm});
            skLineSegment(sketch, "E477.MirrorCS", {"start": v(45.67, -10.9) * mm, "end": v(48.04, -15) * mm});
            skLineSegment(sketch, "E478.MirrorCS", {"start": v(-19.69, -5.9) * mm, "end": v(-22.05, -10) * mm});
            skLineSegment(sketch, "E479.MirrorCS", {"start": v(-39.38, 0) * mm, "end": v(-37, -4.1) * mm});
            skLineSegment(sketch, "E480.MirrorCS", {"start": v(-30.76, -48.58) * mm, "end": v(-32.27, -45.96) * mm});
            skLineSegment(sketch, "E481.MirrorCS", {"start": v(-37, -25.96) * mm, "end": v(-39.38, -30.06) * mm});
            skLineSegment(sketch, "E482.MirrorCS", {"start": v(-3.93, -25) * mm, "end": v(-6.3, -20.9) * mm});
            skLineSegment(sketch, "E483.MirrorCS", {"start": v(11.03, -20.9) * mm, "end": v(13.4, -25) * mm});
            skLineSegment(sketch, "E484.MirrorCS", {"start": v(21.25, -35.06) * mm, "end": v(23.61, -30.96) * mm});
            skLineSegment(sketch, "E485.MirrorCS", {"start": v(40.94, -19.1) * mm, "end": v(45.67, -19.1) * mm});
            skLineSegment(sketch, "E486.MirrorCS", {"start": v(-22.05, -30.06) * mm, "end": v(-19.69, -34.16) * mm});
            skLineSegment(sketch, "E487.MirrorCS", {"start": v(47.23, 0) * mm, "end": v(49.6, -4.1) * mm});
            skLineSegment(sketch, "E488.MirrorCS", {"start": v(2.37, -15.9) * mm, "end": v(4.73, -20) * mm});
            skLineSegment(sketch, "E489.MirrorCS", {"start": v(23.61, -0.9) * mm, "end": v(28.35, -0.9) * mm});
            skLineSegment(sketch, "E490.MirrorCS", {"start": v(14.95, -45.96) * mm, "end": v(19.69, -45.96) * mm});
            skLineSegment(sketch, "E491.MirrorCS", {"start": v(12.59, -30.06) * mm, "end": v(14.95, -34.16) * mm});
            skLineSegment(sketch, "E492.MirrorCS", {"start": v(-14.95, -35.96) * mm, "end": v(-19.69, -35.96) * mm});
            skLineSegment(sketch, "E493.MirrorCS", {"start": v(11.03, -0.9) * mm, "end": v(13.4, -5) * mm});
            skLineSegment(sketch, "E494.MirrorCS", {"start": v(-13.4, -15) * mm, "end": v(-11.03, -19.1) * mm});
            skLineSegment(sketch, "E495.MirrorCS", {"start": v(28.35, -30.96) * mm, "end": v(30.72, -35.06) * mm});
            skLineSegment(sketch, "E496.MirrorCS", {"start": v(-23.61, -19.1) * mm, "end": v(-28.35, -19.1) * mm});
            skLineSegment(sketch, "E497.MirrorCS", {"start": v(-4.73, -40.06) * mm, "end": v(-2.37, -44.16) * mm});
            skLineSegment(sketch, "E498.MirrorCS", {"start": v(49.6, -15.9) * mm, "end": v(54.33, -15.9) * mm});
            skLineSegment(sketch, "E499.MirrorCS", {"start": v(3.93, -15) * mm, "end": v(6.3, -19.1) * mm});
            skLineSegment(sketch, "E500.MirrorCS", {"start": v(-54.33, -15.9) * mm, "end": v(-54.94, -16.96) * mm});
            skLineSegment(sketch, "E501.MirrorCS", {"start": v(13.4, -15) * mm, "end": v(11.03, -19.1) * mm});
            skLineSegment(sketch, "E502.MirrorCS", {"start": v(38.57, -25) * mm, "end": v(40.94, -20.9) * mm});
            skLineSegment(sketch, "E503.MirrorCS", {"start": v(-39.38, -30.06) * mm, "end": v(-37, -34.16) * mm});
            skLineSegment(sketch, "E504.MirrorCS", {"start": v(-6.3, -30.96) * mm, "end": v(-11.03, -30.96) * mm});
            skLineSegment(sketch, "E505.MirrorCS", {"start": v(-47.23, -30.06) * mm, "end": v(-49.6, -25.96) * mm});
            skLineSegment(sketch, "E506.MirrorCS", {"start": v(-38.57, -25) * mm, "end": v(-40.94, -29.1) * mm});
            skLineSegment(sketch, "E507.MirrorCS", {"start": v(-32.27, -24.1) * mm, "end": v(-37, -24.1) * mm});
            skLineSegment(sketch, "E508.MirrorCS", {"start": v(-19.69, -45.96) * mm, "end": v(-22.05, -50.06) * mm});
            skLineSegment(sketch, "E509.MirrorCS", {"start": v(28.35, -10.9) * mm, "end": v(30.72, -15) * mm});
            skLineSegment(sketch, "E510.MirrorCS", {"start": v(14.95, -5.9) * mm, "end": v(19.69, -5.9) * mm});
            skLineSegment(sketch, "E511.MirrorCS", {"start": v(-22.48, -52.92) * mm, "end": v(-23.61, -50.96) * mm});
            skLineSegment(sketch, "E512.MirrorCS", {"start": v(13.4, -25) * mm, "end": v(11.03, -29.1) * mm});
            skLineSegment(sketch, "E513.MirrorCS", {"start": v(-6.3, -10.9) * mm, "end": v(-11.03, -10.9) * mm});
            skLineSegment(sketch, "E514.MirrorCS", {"start": v(-22.05, -20) * mm, "end": v(-19.69, -24.1) * mm});
            skLineSegment(sketch, "E515.MirrorCS", {"start": v(14.95, -24.1) * mm, "end": v(19.69, -24.1) * mm});
            skLineSegment(sketch, "E516.MirrorCS", {"start": v(29.9, 0) * mm, "end": v(32.27, -4.1) * mm});
            skLineSegment(sketch, "E517.MirrorCS", {"start": v(-22.05, -10) * mm, "end": v(-19.69, -14.1) * mm});
            skLineSegment(sketch, "E518.MirrorCS", {"start": v(-30.72, -5) * mm, "end": v(-28.35, -9.1) * mm});
            skLineSegment(sketch, "E519.MirrorCS", {"start": v(29.9, -30.06) * mm, "end": v(32.27, -25.96) * mm});
            skLineSegment(sketch, "E520.MirrorCS", {"start": v(-40.94, -19.1) * mm, "end": v(-45.67, -19.1) * mm});
            skLineSegment(sketch, "E521.MirrorCS", {"start": v(14.95, -14.1) * mm, "end": v(19.69, -14.1) * mm});
            skLineSegment(sketch, "E522.MirrorCS", {"start": v(21.25, -25) * mm, "end": v(23.61, -20.9) * mm});
            skLineSegment(sketch, "E523.MirrorCS", {"start": v(21.25, -5) * mm, "end": v(23.61, -0.9) * mm});
            skLineSegment(sketch, "E524.MirrorCS", {"start": v(32.27, -45.96) * mm, "end": v(34.56, -45.96) * mm});
            skLineSegment(sketch, "E525.MirrorCS", {"start": v(-48.04, -25) * mm, "end": v(-45.67, -29.1) * mm});
            skLineSegment(sketch, "E526.MirrorCS", {"start": v(-40.94, -9.1) * mm, "end": v(-45.67, -9.1) * mm});
            skLineSegment(sketch, "E527.MirrorCS", {"start": v(-2.37, -45.96) * mm, "end": v(-4.73, -50.06) * mm});
            skLineSegment(sketch, "E528.MirrorCS", {"start": v(-12.59, -30.06) * mm, "end": v(-14.95, -25.96) * mm});
            skLineSegment(sketch, "E529.MirrorCS", {"start": v(49.6, -14.1) * mm, "end": v(54.33, -14.1) * mm});
            skLineSegment(sketch, "E530.MirrorCS", {"start": v(-3.93, -5) * mm, "end": v(-6.3, -0.9) * mm});
            skLineSegment(sketch, "E531.MirrorCS", {"start": v(-29.9, -30.06) * mm, "end": v(-32.27, -34.16) * mm});
            skLineSegment(sketch, "E532.MirrorCS", {"start": v(-29.9, 0) * mm, "end": v(-32.27, -4.1) * mm});
            skLineSegment(sketch, "E533.MirrorCS", {"start": v(3.93, -35.06) * mm, "end": v(6.3, -30.96) * mm});
            skLineSegment(sketch, "E534.MirrorCS", {"start": v(13.4, -55.06) * mm, "end": v(12.82, -56.05) * mm});
            skLineSegment(sketch, "E535.MirrorCS", {"start": v(12.59, -50.06) * mm, "end": v(14.95, -54.16) * mm});
            skLineSegment(sketch, "E536.MirrorCS", {"start": v(23.61, -20.9) * mm, "end": v(28.35, -20.9) * mm});
            skLineSegment(sketch, "E537.MirrorCS", {"start": v(-54.33, -5.9) * mm, "end": v(-56.64, -9.9) * mm});
            skLineSegment(sketch, "E538.MirrorCS", {"start": v(19.69, -5.9) * mm, "end": v(22.05, -10) * mm});
            skLineSegment(sketch, "E539.MirrorCS", {"start": v(29.9, -30.06) * mm, "end": v(32.27, -34.16) * mm});
            skLineSegment(sketch, "E540.MirrorCS", {"start": v(6.3, -49.16) * mm, "end": v(11.03, -49.16) * mm});
            skLineSegment(sketch, "E541.MirrorCS", {"start": v(-23.61, -39.16) * mm, "end": v(-28.35, -39.16) * mm});
            skLineSegment(sketch, "E542.MirrorCS", {"start": v(19.69, -35.96) * mm, "end": v(22.05, -40.06) * mm});
            skLineSegment(sketch, "E543.MirrorCS", {"start": v(47.23, -10) * mm, "end": v(49.6, -14.1) * mm});
            skLineSegment(sketch, "E544.MirrorCS", {"start": v(3.93, -45.06) * mm, "end": v(6.3, -49.16) * mm});
            skLineSegment(sketch, "E545.MirrorCS", {"start": v(-32.27, -25.96) * mm, "end": v(-37, -25.96) * mm});
            skLineSegment(sketch, "E546.MirrorCS", {"start": v(39.38, 0) * mm, "end": v(37, -4.1) * mm});
            skLineSegment(sketch, "E547.MirrorCS", {"start": v(-4.73, -30) * mm, "end": v(-2.37, -34.1) * mm});
            skLineSegment(sketch, "E548.MirrorCS", {"start": v(38.57, -35.06) * mm, "end": v(40.94, -30.96) * mm});
            skLineSegment(sketch, "E549.MirrorCS", {"start": v(-30.72, -35.06) * mm, "end": v(-28.35, -39.16) * mm});
            skLineSegment(sketch, "E550.MirrorCS", {"start": v(-47.23, 0) * mm, "end": v(-49.6, -4.1) * mm});
            skLineSegment(sketch, "E551.MirrorCS", {"start": v(-38.57, -5) * mm, "end": v(-40.94, -9.1) * mm});
            skLineSegment(sketch, "E552.MirrorCS", {"start": v(22.48, -52.92) * mm, "end": v(23.61, -50.96) * mm});
            skLineSegment(sketch, "E553.MirrorCS", {"start": v(-49.6, -15.9) * mm, "end": v(-54.33, -15.9) * mm});
            skLineSegment(sketch, "E554.MirrorCS", {"start": v(23.61, -10.9) * mm, "end": v(28.35, -10.9) * mm});
            skLineSegment(sketch, "E555.MirrorCS", {"start": v(21.25, -15) * mm, "end": v(23.61, -19.1) * mm});
            skLineSegment(sketch, "E556.MirrorCS", {"start": v(40.94, -0.9) * mm, "end": v(45.67, -0.9) * mm});
            skLineSegment(sketch, "E557.MirrorCS", {"start": v(-56.59, -10.2) * mm, "end": v(-54.33, -14.1) * mm});
            skLineSegment(sketch, "E558.MirrorCS", {"start": v(-19.69, -35.96) * mm, "end": v(-22.05, -40.06) * mm});
            skLineSegment(sketch, "E559.MirrorCS", {"start": v(-14.95, -34.16) * mm, "end": v(-19.69, -34.16) * mm});
            skLineSegment(sketch, "E560.MirrorCS", {"start": v(-37, -5.9) * mm, "end": v(-39.38, -10) * mm});
            skLineSegment(sketch, "E561.MirrorCS", {"start": v(21.25, -5) * mm, "end": v(23.61, -9.1) * mm});
            skLineSegment(sketch, "E562.MirrorCS", {"start": v(-45.67, -10.9) * mm, "end": v(-48.04, -15) * mm});
            skLineSegment(sketch, "E563.MirrorCS", {"start": v(6.3, -0.9) * mm, "end": v(11.03, -0.9) * mm});
            skLineSegment(sketch, "E564.MirrorCS", {"start": v(-19.69, -15.9) * mm, "end": v(-22.05, -20) * mm});
            skLineSegment(sketch, "E565.MirrorCS", {"start": v(-32.27, -14.1) * mm, "end": v(-37, -14.1) * mm});
            skLineSegment(sketch, "E566.MirrorCS", {"start": v(-40.94, -39.16) * mm, "end": v(-42.1, -39.16) * mm});
            skLineSegment(sketch, "E567.MirrorCS", {"start": v(-47.23, -20) * mm, "end": v(-49.6, -24.1) * mm});
            skLineSegment(sketch, "E568.MirrorCS", {"start": v(-3.93, -35.06) * mm, "end": v(-6.3, -30.96) * mm});
            skLineSegment(sketch, "E569.MirrorCS", {"start": v(-29.9, -20) * mm, "end": v(-32.27, -15.9) * mm});
            skLineSegment(sketch, "E570.MirrorCS", {"start": v(14.95, -15.9) * mm, "end": v(19.69, -15.9) * mm});
            skLineSegment(sketch, "E571.MirrorCS", {"start": v(-38.57, -15) * mm, "end": v(-40.94, -10.9) * mm});
            skLineSegment(sketch, "E572.MirrorCS", {"start": v(47.23, -20) * mm, "end": v(49.6, -24.1) * mm});
            skLineSegment(sketch, "E573.MirrorCS", {"start": v(4.73, -50.06) * mm, "end": v(2.37, -54.16) * mm});
            skLineSegment(sketch, "E574.MirrorCS", {"start": v(12.59, -50.06) * mm, "end": v(14.95, -45.96) * mm});
            skLineSegment(sketch, "E575.MirrorCS", {"start": v(39.38, -10) * mm, "end": v(37, -14.1) * mm});
            skLineSegment(sketch, "E576.MirrorCS", {"start": v(-3.93, -15) * mm, "end": v(-6.3, -19.1) * mm});
            skLineSegment(sketch, "E577.MirrorCS", {"start": v(-49.6, -24.1) * mm, "end": v(-52.2, -24.1) * mm});
            skLineSegment(sketch, "E578.MirrorCS", {"start": v(6.3, -30.96) * mm, "end": v(11.03, -30.96) * mm});
            skLineSegment(sketch, "E579.MirrorCS", {"start": v(-4.73, -50.06) * mm, "end": v(-2.37, -54.16) * mm});
            skLineSegment(sketch, "E580.MirrorCS", {"start": v(19.69, -45.96) * mm, "end": v(22.05, -50.06) * mm});
            skLineSegment(sketch, "E581.MirrorCS", {"start": v(3.93, -25) * mm, "end": v(6.3, -20.9) * mm});
            skLineSegment(sketch, "E582.MirrorCS", {"start": v(-49.6, -14.1) * mm, "end": v(-54.33, -14.1) * mm});
            skLineSegment(sketch, "E583.MirrorCS", {"start": v(21.25, -45.06) * mm, "end": v(23.61, -49.16) * mm});
            skLineSegment(sketch, "E584.MirrorCS", {"start": v(-12.59, -40.06) * mm, "end": v(-14.95, -35.96) * mm});
            skLineSegment(sketch, "E585.MirrorCS", {"start": v(-13.4, -55.06) * mm, "end": v(-12.82, -56.05) * mm});
            skLineSegment(sketch, "E586.MirrorCS", {"start": v(6.3, -39.16) * mm, "end": v(11.03, -39.16) * mm});
            skLineSegment(sketch, "E587.MirrorCS", {"start": v(47.23, -10) * mm, "end": v(49.6, -5.9) * mm});
            skLineSegment(sketch, "E588.MirrorCS", {"start": v(11.03, -40.96) * mm, "end": v(13.4, -45.06) * mm});
            skLineSegment(sketch, "E589.MirrorCS", {"start": v(-11.03, -20.9) * mm, "end": v(-13.4, -25) * mm});
            skLineSegment(sketch, "E590.MirrorCS", {"start": v(55.9, -5) * mm, "end": v(57.07, -7.03) * mm});
            skLineSegment(sketch, "E591.MirrorCS", {"start": v(2.37, -5.9) * mm, "end": v(4.73, -10) * mm});
            skLineSegment(sketch, "E592.MirrorCS", {"start": v(19.69, -15.9) * mm, "end": v(22.05, -20) * mm});
            skLineSegment(sketch, "E593.MirrorCS", {"start": v(14.95, -25.96) * mm, "end": v(19.69, -25.96) * mm});
            skLineSegment(sketch, "E594.MirrorCS", {"start": v(38.57, -15) * mm, "end": v(40.94, -19.1) * mm});
            skLineSegment(sketch, "E595.MirrorCS", {"start": v(-29.9, -10) * mm, "end": v(-32.27, -5.9) * mm});
            skLineSegment(sketch, "E596.MirrorCS", {"start": v(-4.73, 0) * mm, "end": v(-2.37, -4.1) * mm});
            skLineSegment(sketch, "E597.MirrorCS", {"start": v(28.35, -20.9) * mm, "end": v(30.72, -25) * mm});
            skLineSegment(sketch, "E598.MirrorCS", {"start": v(-11.03, -50.96) * mm, "end": v(-13.4, -55.06) * mm});
            skLineSegment(sketch, "E599.MirrorCS", {"start": v(-14.95, -25.96) * mm, "end": v(-19.69, -25.96) * mm});
            skLineSegment(sketch, "E600.MirrorCS", {"start": v(-28.35, -10.9) * mm, "end": v(-30.72, -15) * mm});
            skLineSegment(sketch, "E601.MirrorCS", {"start": v(-21.25, -35.06) * mm, "end": v(-23.61, -39.16) * mm});
            skLineSegment(sketch, "E602.MirrorCS", {"start": v(-3.93, -15) * mm, "end": v(-6.3, -10.9) * mm});
            skLineSegment(sketch, "E603.MirrorCS", {"start": v(-40.94, -20.9) * mm, "end": v(-45.67, -20.9) * mm});
            skLineSegment(sketch, "E604.MirrorCS", {"start": v(4.73, -30) * mm, "end": v(2.37, -34.1) * mm});
            skLineSegment(sketch, "E605.MirrorCS", {"start": v(-32.27, -15.9) * mm, "end": v(-37, -15.9) * mm});
            skLineSegment(sketch, "E606.MirrorCS", {"start": v(-22.05, -50.06) * mm, "end": v(-19.79, -53.99) * mm});
            skLineSegment(sketch, "E607.MirrorCS", {"start": v(-45.67, -30.96) * mm, "end": v(-46.96, -33.18) * mm});
            skLineSegment(sketch, "E608.MirrorCS", {"start": v(-2.37, -55.96) * mm, "end": v(-3.2, -57.41) * mm});
            skLineSegment(sketch, "E609.MirrorCS", {"start": v(48.04, -5) * mm, "end": v(45.67, -9.1) * mm});
            skLineSegment(sketch, "E610.MirrorCS", {"start": v(-2.37, -25.9) * mm, "end": v(-4.73, -30) * mm});
            skLineSegment(sketch, "E611.MirrorCS", {"start": v(11.03, -30.96) * mm, "end": v(13.4, -35.06) * mm});
            skLineSegment(sketch, "E612.MirrorCS", {"start": v(12.59, -40.06) * mm, "end": v(14.95, -35.96) * mm});
            skLineSegment(sketch, "E613.MirrorCS", {"start": v(-3.93, -35.06) * mm, "end": v(-6.3, -39.16) * mm});
            skLineSegment(sketch, "E614.MirrorCS", {"start": v(48.04, -25) * mm, "end": v(45.67, -29.1) * mm});
            skLineSegment(sketch, "E615.MirrorCS", {"start": v(-38.57, -35.06) * mm, "end": v(-40.94, -39.16) * mm});
            skLineSegment(sketch, "E616.MirrorCS", {"start": v(23.61, -50.96) * mm, "end": v(26.64, -50.96) * mm});
            skLineSegment(sketch, "E617.MirrorCS", {"start": v(22.05, -40.06) * mm, "end": v(19.69, -44.16) * mm});
            skLineSegment(sketch, "E618.MirrorCS", {"start": v(12.59, -10) * mm, "end": v(14.95, -14.1) * mm});
            skLineSegment(sketch, "E619.MirrorCS", {"start": v(29.9, -20) * mm, "end": v(32.27, -15.9) * mm});
            skLineSegment(sketch, "E620.MirrorCS", {"start": v(4.73, 0) * mm, "end": v(2.37, -4.1) * mm});
            skLineSegment(sketch, "E621.MirrorCS", {"start": v(-28.35, -20.9) * mm, "end": v(-30.72, -25) * mm});
            skLineSegment(sketch, "E622.MirrorCS", {"start": v(23.61, -40.96) * mm, "end": v(28.35, -40.96) * mm});
            skLineSegment(sketch, "E623.MirrorCS", {"start": v(-23.61, -10.9) * mm, "end": v(-28.35, -10.9) * mm});
            skLineSegment(sketch, "E624.MirrorCS", {"start": v(23.61, -49.16) * mm, "end": v(28.35, -49.16) * mm});
            skLineSegment(sketch, "E625.MirrorCS", {"start": v(54.33, -5.9) * mm, "end": v(56.64, -9.9) * mm});
            skLineSegment(sketch, "E626.MirrorCS", {"start": v(32.27, -24.1) * mm, "end": v(37, -24.1) * mm});
            skLineSegment(sketch, "E627.MirrorCS", {"start": v(38.57, -25) * mm, "end": v(40.94, -29.1) * mm});
            skLineSegment(sketch, "E628.MirrorCS", {"start": v(-45.67, -20.9) * mm, "end": v(-48.04, -25) * mm});
            skLineSegment(sketch, "E629.MirrorCS", {"start": v(21.25, -45.06) * mm, "end": v(23.61, -40.96) * mm});
            skLineSegment(sketch, "E630.MirrorCS", {"start": v(47.23, -30.06) * mm, "end": v(49.6, -25.96) * mm});
            skLineSegment(sketch, "E631.MirrorCS", {"start": v(-14.95, -24.1) * mm, "end": v(-19.69, -24.1) * mm});
            skLineSegment(sketch, "E632.MirrorCS", {"start": v(23.61, -19.1) * mm, "end": v(28.35, -19.1) * mm});
            skLineSegment(sketch, "E633.MirrorCS", {"start": v(3.93, -25) * mm, "end": v(6.3, -29.1) * mm});
            skLineSegment(sketch, "E634.MirrorCS", {"start": v(45.67, -30.96) * mm, "end": v(46.96, -33.18) * mm});
            skLineSegment(sketch, "E635.MirrorCS", {"start": v(23.61, -30.96) * mm, "end": v(28.35, -30.96) * mm});
            skLineSegment(sketch, "E636.MirrorCS", {"start": v(6.3, -40.96) * mm, "end": v(11.03, -40.96) * mm});
            skPoint(sketch, "E637.orphan", {"position": v(-56.7, -10) * mm});
            skLineSegment(sketch, "E638.MirrorCS", {"start": v(-22.48, 52.92) * mm, "end": v(-23.61, 50.96) * mm});
            skArc(sketch, "E639.trimOffspring", {"start": v(-42.1, 39.16) * mm, "mid": v(-44.63, 36.25) * mm, "end": v(-46.96, 33.18) * mm});
            skArc(sketch, "E640.trimOffspring", {"start": v(-30.76, 48.58) * mm, "mid": v(-32.68, 47.3) * mm, "end": v(-34.56, 45.96) * mm});
            skArc(sketch, "E641.trimOffspring", {"start": v(-22.48, 52.92) * mm, "mid": v(-24.58, 51.98) * mm, "end": v(-26.64, 50.96) * mm});
            skArc(sketch, "E642.trimOffspring", {"start": v(-19.32, 54.16) * mm, "mid": v(-19.55, 54.07) * mm, "end": v(-19.79, 53.99) * mm});
            skArc(sketch, "E643.trimOffspring", {"start": v(-5.2, 57.26) * mm, "mid": v(-9.03, 56.79) * mm, "end": v(-12.82, 56.05) * mm});
            skArc(sketch, "E644.trimOffspring", {"start": v(12.82, 56.05) * mm, "mid": v(9.03, 56.79) * mm, "end": v(5.2, 57.26) * mm});
            skArc(sketch, "E645.trimOffspring", {"start": v(19.79, 53.99) * mm, "mid": v(19.55, 54.07) * mm, "end": v(19.32, 54.16) * mm});
            skArc(sketch, "E646.trimOffspring", {"start": v(26.64, 50.96) * mm, "mid": v(24.58, 51.98) * mm, "end": v(22.48, 52.92) * mm});
            skArc(sketch, "E647.trimOffspring", {"start": v(34.56, 45.96) * mm, "mid": v(32.68, 47.3) * mm, "end": v(30.76, 48.58) * mm});
            skArc(sketch, "E648.trimOffspring", {"start": v(37.18, 43.86) * mm, "mid": v(37, 44.01) * mm, "end": v(36.83, 44.16) * mm});
            skArc(sketch, "E649.trimOffspring", {"start": v(46.96, 33.18) * mm, "mid": v(44.63, 36.25) * mm, "end": v(42.1, 39.16) * mm});
            skArc(sketch, "E650.trimOffspring", {"start": v(51.3, 25.96) * mm, "mid": v(49.77, 28.8) * mm, "end": v(48.08, 31.53) * mm});
            skArc(sketch, "E651.trimOffspring", {"start": v(54.94, 16.96) * mm, "mid": v(53.7, 20.57) * mm, "end": v(52.2, 24.1) * mm});
            skArc(sketch, "E652.trimOffspring", {"start": v(56.64, 9.9) * mm, "mid": v(56.62, 10.05) * mm, "end": v(56.59, 10.2) * mm});
            skArc(sketch, "E653.trimOffspring", {"start": v(57.07, -7.03) * mm, "mid": v(57.31, -4.67) * mm, "end": v(57.45, -2.3) * mm});
            skArc(sketch, "E654.trimOffspring", {"start": v(52.2, -24.1) * mm, "mid": v(53.7, -20.57) * mm, "end": v(54.94, -16.96) * mm});
            skArc(sketch, "E655.trimOffspring", {"start": v(56.59, -10.2) * mm, "mid": v(56.62, -10.05) * mm, "end": v(56.64, -9.9) * mm});
            skArc(sketch, "E656.trimOffspring", {"start": v(48.08, -31.53) * mm, "mid": v(49.77, -28.8) * mm, "end": v(51.3, -25.96) * mm});
            skArc(sketch, "E657.trimOffspring", {"start": v(40.66, -40.66) * mm, "mid": v(43.97, -37.06) * mm, "end": v(46.96, -33.18) * mm});
            skArc(sketch, "E658.trimOffspring", {"start": v(30.76, -48.58) * mm, "mid": v(32.68, -47.3) * mm, "end": v(34.56, -45.96) * mm});
            skArc(sketch, "E659.trimOffspring", {"start": v(22.48, -52.92) * mm, "mid": v(24.58, -51.98) * mm, "end": v(26.64, -50.96) * mm});
            skArc(sketch, "E660.trimOffspring", {"start": v(19.32, -54.16) * mm, "mid": v(19.55, -54.07) * mm, "end": v(19.79, -53.99) * mm});
            skArc(sketch, "E661.trimOffspring", {"start": v(5.2, -57.26) * mm, "mid": v(9.03, -56.79) * mm, "end": v(12.82, -56.05) * mm});
            skArc(sketch, "E662.trimOffspring", {"start": v(-3.2, -57.41) * mm, "mid": v(0, -57.5) * mm, "end": v(3.2, -57.41) * mm});
            skArc(sketch, "E663.trimOffspring", {"start": v(-12.82, -56.05) * mm, "mid": v(-9.03, -56.79) * mm, "end": v(-5.2, -57.26) * mm});
            skArc(sketch, "E664.trimOffspring", {"start": v(-26.64, -50.96) * mm, "mid": v(-24.58, -51.98) * mm, "end": v(-22.48, -52.92) * mm});
            skArc(sketch, "E665.trimOffspring", {"start": v(-37.18, -43.86) * mm, "mid": v(-37, -44.01) * mm, "end": v(-36.83, -44.16) * mm});
            skArc(sketch, "E666.trimOffspring", {"start": v(-46.96, -33.18) * mm, "mid": v(-44.63, -36.25) * mm, "end": v(-42.1, -39.16) * mm});
            skArc(sketch, "E667.trimOffspring", {"start": v(-51.3, -25.96) * mm, "mid": v(-49.77, -28.8) * mm, "end": v(-48.08, -31.53) * mm});
            skArc(sketch, "E668.trimOffspring", {"start": v(-54.94, -16.96) * mm, "mid": v(-53.7, -20.57) * mm, "end": v(-52.2, -24.1) * mm});
            skArc(sketch, "E669.trimOffspring", {"start": v(-56.64, -9.9) * mm, "mid": v(-56.62, -10.05) * mm, "end": v(-56.59, -10.2) * mm});
            skArc(sketch, "E670.trimOffspring", {"start": v(-57.45, -2.3) * mm, "mid": v(-57.31, -4.67) * mm, "end": v(-57.07, -7.03) * mm});
            skArc(sketch, "E671.trimOffspring", {"start": v(-19.79, -53.99) * mm, "mid": v(-19.55, -54.07) * mm, "end": v(-19.32, -54.16) * mm});
            skArc(sketch, "E672", {"start": v(-34.56, -45.96) * mm, "mid": v(-32.68, -47.3) * mm, "end": v(-30.76, -48.58) * mm});
            skArc(sketch, "E673.trimOffspring", {"start": v(-57.07, 7.03) * mm, "mid": v(-57.31, 4.67) * mm, "end": v(-57.45, 2.3) * mm});
            skArc(sketch, "E674.trimOffspring", {"start": v(-56.59, 10.2) * mm, "mid": v(-56.62, 10.05) * mm, "end": v(-56.64, 9.9) * mm});
            skArc(sketch, "E675.trimOffspring", {"start": v(-52.2, 24.1) * mm, "mid": v(-53.7, 20.57) * mm, "end": v(-54.94, 16.96) * mm});
            skArc(sketch, "E676.trimOffspring", {"start": v(-48.08, 31.53) * mm, "mid": v(-49.77, 28.8) * mm, "end": v(-51.3, 25.96) * mm});
            skArc(sketch, "E677", {"start": v(-37.18, 43.86) * mm, "mid": v(-37, 44.01) * mm, "end": v(-36.83, 44.16) * mm});
            skArc(sketch, "E678", {"start": v(36.83, -44.16) * mm, "mid": v(37, -44.01) * mm, "end": v(37.18, -43.86) * mm});
            skPoint(sketch, "E679", {"position": v(-52.5, 52.5) * mm});
            skPoint(sketch, "E680", {"position": v(52.74, 53.66) * mm});
            skPoint(sketch, "E681", {"position": v(52.74, -52.34) * mm});
            skPoint(sketch, "E682", {"position": v(-52.26, -52.34) * mm});
            skCircle(sketch, "E683", {"center": v(-52.5, 52.5) * mm, "radius": 4.5 * mm});
            skCircle(sketch, "E684", {"center": v(52.74, 53.66) * mm, "radius": 4.5 * mm});
            skCircle(sketch, "E685", {"center": v(-52.26, -52.34) * mm, "radius": 4.5 * mm});
            skCircle(sketch, "E686", {"center": v(52.74, -52.34) * mm, "radius": 4.5 * mm});
            skArc(sketch, "E687.0", {"start": v(-61, 71) * mm, "mid": v(-68.07, 68.07) * mm, "end": v(-71, 61) * mm});
            skLineSegment(sketch, "E687.1", {"start": v(-71, 61) * mm, "end": v(-71, -87.5) * mm});
            skLineSegment(sketch, "E687.2", {"start": v(-61, 71) * mm, "end": v(61, 71) * mm});
            skArc(sketch, "E687.3", {"start": v(-71, -87.5) * mm, "mid": v(-68.07, -94.57) * mm, "end": v(-61, -97.5) * mm});
            skArc(sketch, "E687.4", {"start": v(71, 61) * mm, "mid": v(68.07, 68.07) * mm, "end": v(61, 71) * mm});
            skLineSegment(sketch, "E687.5", {"start": v(71, 61) * mm, "end": v(71, -87.5) * mm});
            skArc(sketch, "E687.6", {"start": v(61, -97.5) * mm, "mid": v(68.07, -94.57) * mm, "end": v(71, -87.5) * mm});
            skLineSegment(sketch, "E687.7", {"start": v(-61, -97.5) * mm, "end": v(61, -97.5) * mm});
            skCircle(sketch, "E688", {"center": v(-61, 61) * mm, "radius": 2 * mm});
            skCircle(sketch, "E689", {"center": v(-61, -87.5) * mm, "radius": 2 * mm});
            skCircle(sketch, "E690.MirrorC", {"center": v(61, -87.5) * mm, "radius": 2 * mm});
            skCircle(sketch, "E691.MirrorC", {"center": v(61, 61) * mm, "radius": 2 * mm});
            skArc(sketch, "E692.MirrorCS", {"start": v(3.2, -57.41) * mm, "mid": v(0, -57.5) * mm, "end": v(-3.2, -57.41) * mm});
            skLineSegment(sketch, "E693.MirrorCS", {"start": v(-2.37, 55.96) * mm, "end": v(-3.2, 57.41) * mm});
            skLineSegment(sketch, "E694.MirrorCS", {"start": v(2.37, 55.96) * mm, "end": v(3.2, 57.41) * mm});
            skLineSegment(sketch, "E695.MirrorCS", {"start": v(0, 55.96) * mm, "end": v(-2.37, 55.96) * mm});
            skLineSegment(sketch, "E696.MirrorCS", {"start": v(0, 55.96) * mm, "end": v(2.37, 55.96) * mm});
            skArc(sketch, "E697.MirrorCS", {"start": v(-3.2, 57.41) * mm, "mid": v(0, 57.5) * mm, "end": v(3.2, 57.41) * mm});
            skArc(sketch, "E698.MirrorCS", {"start": v(3.2, 57.41) * mm, "mid": v(0, 57.5) * mm, "end": v(-3.2, 57.41) * mm});
            skSolve(sketch);
        }
        {
            var Q0;
            Q0=makeQuery(id+"F0.imprint","IMPRINT",FACE,{"disambiguationData":[TD([[makeQuery(id+"F0.imprint","IMPRINT",EDGE,{"derivedFrom":sQuery(id+"F0.wireOp",EDGE,"E16.0")}),-1.0]])]});
            var Q1;
            Q1=makeQuery(id+"F0.imprint","IMPRINT",FACE,{"disambiguationData":[TD([[makeQuery(id+"F0.imprint","IMPRINT",EDGE,{"derivedFrom":sQuery(id+"F0.wireOp",EDGE,"E683")}),1.0]])]});
            var Q2;
            Q2=makeQuery(id+"F0.imprint","IMPRINT",FACE,{"disambiguationData":[TD([[makeQuery(id+"F0.imprint","IMPRINT",EDGE,{"derivedFrom":sQuery(id+"F0.wireOp",EDGE,"E684")}),1.0]])]});
            var Q3;
            Q3=makeQuery(id+"F0.imprint","IMPRINT",FACE,{"disambiguationData":[TD([[makeQuery(id+"F0.imprint","IMPRINT",EDGE,{"derivedFrom":sQuery(id+"F0.wireOp",EDGE,"E686")}),1.0]])]});
            var Q4;
            Q4=makeQuery(id+"F0.imprint","IMPRINT",FACE,{"disambiguationData":[TD([[makeQuery(id+"F0.imprint","IMPRINT",EDGE,{"derivedFrom":sQuery(id+"F0.wireOp",EDGE,"E685")}),1.0]])]});
            extrude(context, id + "F1", {"entities" : qUnion([Q0, Q1, Q2, Q3, Q4]), "depth" : 3 * mm});
        }
        {
            var Q0;
            Q0=makeQuery(id+"F0.imprint","IMPRINT",FACE,{"disambiguationData":[TD([[makeQuery(id+"F0.imprint","IMPRINT",EDGE,{"derivedFrom":sQuery(id+"F0.wireOp",EDGE,"E683")}),1.0]])]});
            var Q1;
            Q1=makeQuery(id+"F0.imprint","IMPRINT",FACE,{"disambiguationData":[TD([[makeQuery(id+"F0.imprint","IMPRINT",EDGE,{"derivedFrom":sQuery(id+"F0.wireOp",EDGE,"E684")}),1.0]])]});
            var Q2;
            Q2=makeQuery(id+"F0.imprint","IMPRINT",FACE,{"disambiguationData":[TD([[makeQuery(id+"F0.imprint","IMPRINT",EDGE,{"derivedFrom":sQuery(id+"F0.wireOp",EDGE,"E686")}),1.0]])]});
            var Q3;
            Q3=makeQuery(id+"F0.imprint","IMPRINT",FACE,{"disambiguationData":[TD([[makeQuery(id+"F0.imprint","IMPRINT",EDGE,{"derivedFrom":sQuery(id+"F0.wireOp",EDGE,"E685")}),1.0]])]});
            extrude(context, id + "F2", {"entities" : qUnion([Q0, Q1, Q2, Q3]), "operationType" : NewBodyOperationType.REMOVE, "depth" : 2 * mm});
        }
    });
